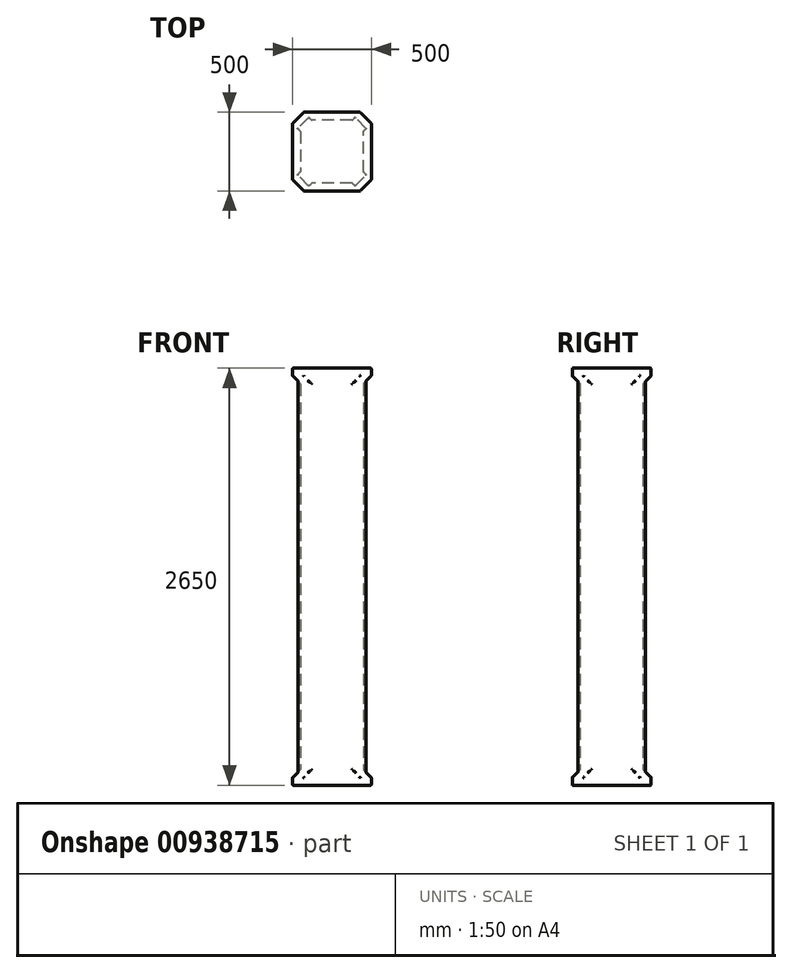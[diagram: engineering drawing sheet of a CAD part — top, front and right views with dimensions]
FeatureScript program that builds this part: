
annotation { "Feature Type Name" : "Feature", "Feature Type Description" : "" }
export const myFeature = defineFeature(function(context is Context, id is Id, definition is map)
    precondition{}
    {
        {
            var Q0;
            Q0=qCreatedBy(makeId("Top.planeOp"),FACE);
            var sketch = newSketch(context, id + "F0", { "sketchPlane" : qUnion([Q0])});
            skLineSegment(sketch, "E0.left", {"start": v(200, 129.29) * mm, "end": v(200, -129.29) * mm});
            skLineSegment(sketch, "E0.right", {"start": v(-200, 129.29) * mm, "end": v(-200, -129.29) * mm});
            skPoint(sketch, "E0.middle", {"position": v(0, 0) * mm});
            skLineSegment(sketch, "E1", {"start": v(-129.29, 200) * mm, "end": v(-146.97, 217.68) * mm});
            skLineSegment(sketch, "E2", {"start": v(-217.68, 146.97) * mm, "end": v(-200, 129.29) * mm});
            skLineSegment(sketch, "E3.1.0", {"start": v(-200, -129.29) * mm, "end": v(-217.68, -146.97) * mm});
            skLineSegment(sketch, "E3.1.3", {"start": v(-146.97, -217.68) * mm, "end": v(-129.29, -200) * mm});
            skLineSegment(sketch, "E3.2.0", {"start": v(129.29, -200) * mm, "end": v(146.97, -217.68) * mm});
            skLineSegment(sketch, "E3.2.3", {"start": v(217.68, -146.97) * mm, "end": v(200, -129.29) * mm});
            skLineSegment(sketch, "E3.3.0", {"start": v(200, 129.29) * mm, "end": v(217.68, 146.97) * mm});
            skLineSegment(sketch, "E3.3.3", {"start": v(146.97, 217.68) * mm, "end": v(129.29, 200) * mm});
            skLineSegment(sketch, "E4", {"start": v(-217.68, 146.97) * mm, "end": v(-146.97, 217.68) * mm});
            skLineSegment(sketch, "E5", {"start": v(0, 0) * mm, "end": v(-182.32, 182.32) * mm});
            skLineSegment(sketch, "E6", {"start": v(-217.68, -146.97) * mm, "end": v(-146.97, -217.68) * mm});
            skLineSegment(sketch, "E7", {"start": v(146.97, 217.68) * mm, "end": v(217.68, 146.97) * mm});
            skLineSegment(sketch, "E8", {"start": v(217.68, -146.97) * mm, "end": v(146.97, -217.68) * mm});
            skLineSegment(sketch, "E9.trimOffspring", {"start": v(129.29, -200) * mm, "end": v(-129.29, -200) * mm});
            skLineSegment(sketch, "E10.trimOffspring", {"start": v(129.29, 200) * mm, "end": v(-129.29, 200) * mm});
            skLineSegment(sketch, "E11", {"start": v(0, 0) * mm, "end": v(182.32, -182.32) * mm});
            skLineSegment(sketch, "E12", {"start": v(0, 0) * mm, "end": v(182.32, 182.32) * mm});
            skLineSegment(sketch, "E13", {"start": v(0, 0) * mm, "end": v(-182.32, -182.32) * mm});
            skSolve(sketch);
        }
        {
            var Q0;
            Q0 = qSketchRegion(id + "F0", true);
            extrude(context, id + "F1", {"entities" : qUnion([Q0]), "depth" : 1325 * mm, "offsetDistance" : 25 * mm});
        }
        {
            var Q0;
            Q0=qCreatedBy(makeId("Top.planeOp"),FACE);
            var sketch = newSketch(context, id + "F2", { "sketchPlane" : qUnion([Q0])});
            skPoint(sketch, "E14.middle", {"position": v(0, 0) * mm});
            skLineSegment(sketch, "E15", {"start": v(-179.29, 250) * mm, "end": v(179.29, 250) * mm});
            skLineSegment(sketch, "E16", {"start": v(179.29, 250) * mm, "end": v(250, 179.29) * mm});
            skLineSegment(sketch, "E17", {"start": v(250, 179.29) * mm, "end": v(250, -179.29) * mm});
            skLineSegment(sketch, "E18", {"start": v(250, -179.29) * mm, "end": v(179.29, -250) * mm});
            skLineSegment(sketch, "E19", {"start": v(179.29, -250) * mm, "end": v(-179.29, -250) * mm});
            skLineSegment(sketch, "E20", {"start": v(-179.29, -250) * mm, "end": v(-250, -179.29) * mm});
            skLineSegment(sketch, "E21", {"start": v(-250, -179.29) * mm, "end": v(-250, 179.29) * mm});
            skLineSegment(sketch, "E22", {"start": v(-250, 179.29) * mm, "end": v(-179.29, 250) * mm});
            skLineSegment(sketch, "E23", {"start": v(-214.64, -214.64) * mm, "end": v(214.64, 214.64) * mm});
            skLineSegment(sketch, "E24", {"start": v(214.64, -214.64) * mm, "end": v(-214.64, 214.64) * mm});
            skSolve(sketch);
        }
        {
            var Q0;
            Q0 = qSketchRegion(id + "F2", true);
            extrude(context, id + "F3", {"entities" : qUnion([Q0]), "depth" : 50 * mm, "offsetDistance" : 25 * mm});
        }
        {
            var Q0;
            Q0=qCreatedBy(makeId("Top.planeOp"),FACE);
            var sketch = newSketch(context, id + "F4", { "sketchPlane" : qUnion([Q0])});
            skLineSegment(sketch, "E25", {"start": v(-129.29, 200) * mm, "end": v(129.29, 200) * mm});
            skLineSegment(sketch, "E26", {"start": v(129.29, 200) * mm, "end": v(200, 129.29) * mm});
            skLineSegment(sketch, "E27", {"start": v(200, 129.29) * mm, "end": v(200, -129.29) * mm});
            skLineSegment(sketch, "E28", {"start": v(-129.29, -200) * mm, "end": v(-200, -129.29) * mm});
            skLineSegment(sketch, "E29", {"start": v(-200, -129.29) * mm, "end": v(-200, 129.29) * mm});
            skLineSegment(sketch, "E30", {"start": v(-200, 129.29) * mm, "end": v(-129.29, 200) * mm});
            skLineSegment(sketch, "E31", {"start": v(-129.29, -200) * mm, "end": v(129.29, -200) * mm});
            skLineSegment(sketch, "E32", {"start": v(129.29, -200) * mm, "end": v(200, -129.29) * mm});
            skLineSegment(sketch, "E33", {"start": v(-164.64, -164.64) * mm, "end": v(164.64, 164.64) * mm});
            skLineSegment(sketch, "E34", {"start": v(-164.64, 164.64) * mm, "end": v(164.64, -164.64) * mm});
            skPoint(sketch, "E35", {"position": v(0, 0) * mm});
            skSolve(sketch);
        }
        {
            var Q0;
            Q0 = qSketchRegion(id + "F4", true);
            extrude(context, id + "F5", {"entities" : qUnion([Q0]), "depth" : 100 * mm, "offsetDistance" : 25 * mm});
        }
        {
            var Q0;
            Q0=makeQuery(id+"F3.opExtrude","CAP_FACE",FACE,{"disambiguationData":[OSD([sQuery(id+"F2.wireOp",EDGE,"E15"),sQuery(id+"F2.wireOp",EDGE,"E16"),sQuery(id+"F2.wireOp",EDGE,"E17"),sQuery(id+"F2.wireOp",EDGE,"E18"),sQuery(id+"F2.wireOp",EDGE,"E19"),sQuery(id+"F2.wireOp",EDGE,"E20"),sQuery(id+"F2.wireOp",EDGE,"E21"),sQuery(id+"F2.wireOp",EDGE,"E22")])],"isStart":false});
            var Q1;
            Q1=makeQuery(id+"F5.opExtrude","CAP_FACE",FACE,{"disambiguationData":[OSD([sQuery(id+"F4.wireOp",EDGE,"E25"),sQuery(id+"F4.wireOp",EDGE,"E26"),sQuery(id+"F4.wireOp",EDGE,"E27"),sQuery(id+"F4.wireOp",EDGE,"E28"),sQuery(id+"F4.wireOp",EDGE,"E29"),sQuery(id+"F4.wireOp",EDGE,"E30"),sQuery(id+"F4.wireOp",EDGE,"E31"),sQuery(id+"F4.wireOp",EDGE,"E32")])],"isStart":false});
            loft(context, id + "F6", {"operationType" : NewBodyOperationType.ADD, "sheetProfilesArray" : [{ "sheetProfileEntities" : qUnion([Q0]) }, { "sheetProfileEntities" : qUnion([Q1]) }]});
        }
        {
            var Q0;
            Q0=makeQuery(id+"F5.opExtrude","SWEPT_BODY",BODY,{"disambiguationData":[OSD([sQuery(id+"F4.wireOp",EDGE,"E25"),sQuery(id+"F4.wireOp",EDGE,"E26"),sQuery(id+"F4.wireOp",EDGE,"E27"),sQuery(id+"F4.wireOp",EDGE,"E28"),sQuery(id+"F4.wireOp",EDGE,"E29"),sQuery(id+"F4.wireOp",EDGE,"E30"),sQuery(id+"F4.wireOp",EDGE,"E31"),sQuery(id+"F4.wireOp",EDGE,"E32")])]});
            var Q1;
            Q1=makeQuery(id+"F3.opExtrude","SWEPT_BODY",BODY,{"disambiguationData":[OSD([sQuery(id+"F2.wireOp",EDGE,"E15"),sQuery(id+"F2.wireOp",EDGE,"E16"),sQuery(id+"F2.wireOp",EDGE,"E17"),sQuery(id+"F2.wireOp",EDGE,"E18"),sQuery(id+"F2.wireOp",EDGE,"E19"),sQuery(id+"F2.wireOp",EDGE,"E20"),sQuery(id+"F2.wireOp",EDGE,"E21"),sQuery(id+"F2.wireOp",EDGE,"E22")])]});
            var Q2;
            Q2=makeQuery(id+"F1.opExtrude","SWEPT_BODY",BODY,{"disambiguationData":[OSD([sQuery(id+"F0.wireOp",EDGE,"E0.left"),sQuery(id+"F0.wireOp",EDGE,"E0.right"),sQuery(id+"F0.wireOp",EDGE,"E1"),sQuery(id+"F0.wireOp",EDGE,"E2"),sQuery(id+"F0.wireOp",EDGE,"E3.1.0"),sQuery(id+"F0.wireOp",EDGE,"E3.1.3"),sQuery(id+"F0.wireOp",EDGE,"E3.2.0"),sQuery(id+"F0.wireOp",EDGE,"E3.2.3"),sQuery(id+"F0.wireOp",EDGE,"E3.3.0"),sQuery(id+"F0.wireOp",EDGE,"E3.3.3"),sQuery(id+"F0.wireOp",EDGE,"E4"),sQuery(id+"F0.wireOp",EDGE,"E6"),sQuery(id+"F0.wireOp",EDGE,"E7"),sQuery(id+"F0.wireOp",EDGE,"E8"),sQuery(id+"F0.wireOp",EDGE,"E9.trimOffspring"),sQuery(id+"F0.wireOp",EDGE,"E10.trimOffspring")])]});
            var Q3;
            Q3=makeQuery(id+"F6.opLoft","SWEPT_BODY",BODY,{"disambiguationData":[OSD([sQuery(id+"F2.wireOp",EDGE,"E15"),sQuery(id+"F2.wireOp",EDGE,"E16"),sQuery(id+"F2.wireOp",EDGE,"E17"),sQuery(id+"F2.wireOp",EDGE,"E18"),sQuery(id+"F2.wireOp",EDGE,"E19"),sQuery(id+"F2.wireOp",EDGE,"E20"),sQuery(id+"F2.wireOp",EDGE,"E21"),sQuery(id+"F2.wireOp",EDGE,"E22"),sQuery(id+"F4.wireOp",EDGE,"E25"),sQuery(id+"F4.wireOp",EDGE,"E26"),sQuery(id+"F4.wireOp",EDGE,"E27"),sQuery(id+"F4.wireOp",EDGE,"E28"),sQuery(id+"F4.wireOp",EDGE,"E29"),sQuery(id+"F4.wireOp",EDGE,"E30"),sQuery(id+"F4.wireOp",EDGE,"E31"),sQuery(id+"F4.wireOp",EDGE,"E32")])]});
            var Q4;
            Q4=makeQuery(id+"F1.opExtrude","CAP_FACE",FACE,{"disambiguationData":[OSD([sQuery(id+"F0.wireOp",EDGE,"E0.left"),sQuery(id+"F0.wireOp",EDGE,"E0.right"),sQuery(id+"F0.wireOp",EDGE,"E1"),sQuery(id+"F0.wireOp",EDGE,"E2"),sQuery(id+"F0.wireOp",EDGE,"E3.1.0"),sQuery(id+"F0.wireOp",EDGE,"E3.1.3"),sQuery(id+"F0.wireOp",EDGE,"E3.2.0"),sQuery(id+"F0.wireOp",EDGE,"E3.2.3"),sQuery(id+"F0.wireOp",EDGE,"E3.3.0"),sQuery(id+"F0.wireOp",EDGE,"E3.3.3"),sQuery(id+"F0.wireOp",EDGE,"E4"),sQuery(id+"F0.wireOp",EDGE,"E6"),sQuery(id+"F0.wireOp",EDGE,"E7"),sQuery(id+"F0.wireOp",EDGE,"E8"),sQuery(id+"F0.wireOp",EDGE,"E9.trimOffspring"),sQuery(id+"F0.wireOp",EDGE,"E10.trimOffspring")])],"isStart":false});
            mirror(context, id + "F7", {"operationType" : NewBodyOperationType.ADD, "entities" : qUnion([Q0, Q1, Q2, Q3]), "mirrorPlane" : qUnion([Q4])});
        }
        {
            var Q0;
            Q0=makeQuery(id+"F5.opExtrude","CAP_FACE",FACE,{"disambiguationData":[OSD([sQuery(id+"F4.wireOp",EDGE,"E25"),sQuery(id+"F4.wireOp",EDGE,"E26"),sQuery(id+"F4.wireOp",EDGE,"E27"),sQuery(id+"F4.wireOp",EDGE,"E28"),sQuery(id+"F4.wireOp",EDGE,"E29"),sQuery(id+"F4.wireOp",EDGE,"E30"),sQuery(id+"F4.wireOp",EDGE,"E31"),sQuery(id+"F4.wireOp",EDGE,"E32")])],"isStart":false});
            var Q1;
            Q1=makeQuery(id+"F5.opExtrude","SWEPT_FACE",FACE,{"disambiguationData":[OSD([sQuery(id+"F4.wireOp",EDGE,"E31")])]});
            var Q2;
            Q2=makeQuery(id+"F5.opExtrude","CAP_EDGE",EDGE,{"disambiguationData":[OSD([sQuery(id+"F4.wireOp",EDGE,"E27")])],"isStart":false});
            var Q3;
            Q3=makeQuery(id+"F3.opExtrude","CAP_FACE",FACE,{"disambiguationData":[OSD([sQuery(id+"F2.wireOp",EDGE,"E15"),sQuery(id+"F2.wireOp",EDGE,"E16"),sQuery(id+"F2.wireOp",EDGE,"E17"),sQuery(id+"F2.wireOp",EDGE,"E18"),sQuery(id+"F2.wireOp",EDGE,"E19"),sQuery(id+"F2.wireOp",EDGE,"E20"),sQuery(id+"F2.wireOp",EDGE,"E21"),sQuery(id+"F2.wireOp",EDGE,"E22")])],"isStart":true});
            var Q4;
            Q4=makeQuery(id+"F3.opExtrude","CAP_FACE",FACE,{"disambiguationData":[OSD([sQuery(id+"F2.wireOp",EDGE,"E15"),sQuery(id+"F2.wireOp",EDGE,"E16"),sQuery(id+"F2.wireOp",EDGE,"E17"),sQuery(id+"F2.wireOp",EDGE,"E18"),sQuery(id+"F2.wireOp",EDGE,"E19"),sQuery(id+"F2.wireOp",EDGE,"E20"),sQuery(id+"F2.wireOp",EDGE,"E21"),sQuery(id+"F2.wireOp",EDGE,"E22")])],"isStart":false});
            var Q5;
            Q5=makeQuery(id+"F3.opExtrude","SWEPT_FACE",FACE,{"disambiguationData":[OSD([sQuery(id+"F2.wireOp",EDGE,"E16")])]});
            var Q6;
            Q6=makeQuery(id+"F3.opExtrude","SWEPT_FACE",FACE,{"disambiguationData":[OSD([sQuery(id+"F2.wireOp",EDGE,"E19")])]});
            var Q7;
            Q7=makeQuery(id+"F3.opExtrude","CAP_EDGE",EDGE,{"disambiguationData":[OSD([sQuery(id+"F2.wireOp",EDGE,"E17")])],"isStart":false});
            var Q8;
            Q8=makeQuery(id+"F3.opExtrude","SWEPT_FACE",FACE,{"disambiguationData":[OSD([sQuery(id+"F2.wireOp",EDGE,"E17")])]});
            var Q9;
            Q9=makeQuery(id+"F3.opExtrude","SWEPT_FACE",FACE,{"disambiguationData":[OSD([sQuery(id+"F2.wireOp",EDGE,"E18")])]});
            var Q10;
            Q10=makeQuery(id+"F3.opExtrude","CAP_EDGE",EDGE,{"disambiguationData":[OSD([sQuery(id+"F2.wireOp",EDGE,"E17")])],"isStart":true});
            var Q11;
            {var subQ0=makeQuery(id+"F1.opExtrude","SWEPT_FACE",FACE,{"disambiguationData":[OSD([sQuery(id+"F0.wireOp",EDGE,"E3.1.0")])]});Q11=makeQuery(id+"F7.boolean.opBoolean","MERGE",FACE,{"derivedFrom":[subQ0,makeQuery(id+"F7.opPattern","COPY",FACE,{"derivedFrom":subQ0,"instanceName":"1"})]});}
            var Q12;
            Q12=makeQuery(id+"F7.opPattern","COPY",EDGE,{"derivedFrom":makeQuery(id+"F3.opExtrude","CAP_EDGE",EDGE,{"disambiguationData":[OSD([sQuery(id+"F2.wireOp",EDGE,"E21")])],"isStart":true}),"instanceName":"1"});
            var Q13;
            {var subQ0=makeQuery(id+"F1.opExtrude","SWEPT_EDGE",EDGE,{"disambiguationData":[OSD([sQuery(id+"F0.wireOp",EDGE,"E3.3.0"),sQuery(id+"F0.wireOp",EDGE,"E7")])]});Q13=makeQuery(id+"F7.boolean.opBoolean","MERGE",EDGE,{"derivedFrom":[subQ0,makeQuery(id+"F7.opPattern","COPY",EDGE,{"derivedFrom":subQ0,"instanceName":"1"})]});}
            var Q14;
            {var subQ0=makeQuery(id+"F1.opExtrude","SWEPT_EDGE",EDGE,{"disambiguationData":[OSD([sQuery(id+"F0.wireOp",EDGE,"E3.2.3"),sQuery(id+"F0.wireOp",EDGE,"E8")])]});Q14=makeQuery(id+"F7.boolean.opBoolean","MERGE",EDGE,{"derivedFrom":[subQ0,makeQuery(id+"F7.opPattern","COPY",EDGE,{"derivedFrom":subQ0,"instanceName":"1"})]});}
            var Q15;
            {var subQ0=makeQuery(id+"F1.opExtrude","SWEPT_FACE",FACE,{"disambiguationData":[OSD([sQuery(id+"F0.wireOp",EDGE,"E3.2.0")])]});Q15=makeQuery(id+"F7.boolean.opBoolean","MERGE",FACE,{"derivedFrom":[subQ0,makeQuery(id+"F7.opPattern","COPY",FACE,{"derivedFrom":subQ0,"instanceName":"1"})]});}
            var Q16;
            {var subQ0=makeQuery(id+"F1.opExtrude","SWEPT_EDGE",EDGE,{"disambiguationData":[OSD([sQuery(id+"F0.wireOp",EDGE,"E3.1.3"),sQuery(id+"F0.wireOp",EDGE,"E6")])]});Q16=makeQuery(id+"F7.boolean.opBoolean","MERGE",EDGE,{"derivedFrom":[subQ0,makeQuery(id+"F7.opPattern","COPY",EDGE,{"derivedFrom":subQ0,"instanceName":"1"})]});}
            var Q17;
            {var subQ0=makeQuery(id+"F1.opExtrude","SWEPT_FACE",FACE,{"disambiguationData":[OSD([sQuery(id+"F0.wireOp",EDGE,"E7")])]});Q17=makeQuery(id+"F7.boolean.opBoolean","MERGE",FACE,{"derivedFrom":[subQ0,makeQuery(id+"F7.opPattern","COPY",FACE,{"derivedFrom":subQ0,"instanceName":"1"})]});}
            var Q18;
            {var subQ0=makeQuery(id+"F1.opExtrude","SWEPT_EDGE",EDGE,{"disambiguationData":[OSD([sQuery(id+"F0.wireOp",EDGE,"E0.left"),sQuery(id+"F0.wireOp",EDGE,"E3.3.0")])]});Q18=makeQuery(id+"F7.boolean.opBoolean","MERGE",EDGE,{"derivedFrom":[subQ0,makeQuery(id+"F7.opPattern","COPY",EDGE,{"derivedFrom":subQ0,"instanceName":"1"})]});}
            var Q19;
            {var subQ0=makeQuery(id+"F1.opExtrude","SWEPT_EDGE",EDGE,{"disambiguationData":[OSD([sQuery(id+"F0.wireOp",EDGE,"E3.1.3"),sQuery(id+"F0.wireOp",EDGE,"E9.trimOffspring")])]});Q19=makeQuery(id+"F7.boolean.opBoolean","MERGE",EDGE,{"derivedFrom":[subQ0,makeQuery(id+"F7.opPattern","COPY",EDGE,{"derivedFrom":subQ0,"instanceName":"1"})]});}
            var Q20;
            Q20=makeQuery(id+"F7.opPattern","COPY",FACE,{"derivedFrom":makeQuery(id+"F3.opExtrude","SWEPT_FACE",FACE,{"disambiguationData":[OSD([sQuery(id+"F2.wireOp",EDGE,"E16")])]}),"instanceName":"1"});
            var Q21;
            {var subQ0=makeQuery(id+"F1.opExtrude","SWEPT_FACE",FACE,{"disambiguationData":[OSD([sQuery(id+"F0.wireOp",EDGE,"E3.1.3")])]});Q21=makeQuery(id+"F7.boolean.opBoolean","MERGE",FACE,{"derivedFrom":[subQ0,makeQuery(id+"F7.opPattern","COPY",FACE,{"derivedFrom":subQ0,"instanceName":"1"})]});}
            var Q22;
            {var subQ0=makeQuery(id+"F1.opExtrude","SWEPT_FACE",FACE,{"disambiguationData":[OSD([sQuery(id+"F0.wireOp",EDGE,"E9.trimOffspring")])]});Q22=makeQuery(id+"F7.boolean.opBoolean","MERGE",FACE,{"derivedFrom":[subQ0,makeQuery(id+"F7.opPattern","COPY",FACE,{"derivedFrom":subQ0,"instanceName":"1"})]});}
            var Q23;
            {var subQ0=makeQuery(id+"F1.opExtrude","SWEPT_FACE",FACE,{"disambiguationData":[OSD([sQuery(id+"F0.wireOp",EDGE,"E3.3.0")])]});Q23=makeQuery(id+"F7.boolean.opBoolean","MERGE",FACE,{"derivedFrom":[subQ0,makeQuery(id+"F7.opPattern","COPY",FACE,{"derivedFrom":subQ0,"instanceName":"1"})]});}
            var Q24;
            {var subQ0=makeQuery(id+"F1.opExtrude","SWEPT_FACE",FACE,{"disambiguationData":[OSD([sQuery(id+"F0.wireOp",EDGE,"E0.left")])]});Q24=makeQuery(id+"F7.boolean.opBoolean","MERGE",FACE,{"derivedFrom":[subQ0,makeQuery(id+"F7.opPattern","COPY",FACE,{"derivedFrom":subQ0,"instanceName":"1"})]});}
            var Q25;
            {var subQ0=makeQuery(id+"F1.opExtrude","SWEPT_FACE",FACE,{"disambiguationData":[OSD([sQuery(id+"F0.wireOp",EDGE,"E6")])]});Q25=makeQuery(id+"F7.boolean.opBoolean","MERGE",FACE,{"derivedFrom":[subQ0,makeQuery(id+"F7.opPattern","COPY",FACE,{"derivedFrom":subQ0,"instanceName":"1"})]});}
            var Q26;
            {var subQ0=makeQuery(id+"F1.opExtrude","SWEPT_EDGE",EDGE,{"disambiguationData":[OSD([sQuery(id+"F0.wireOp",EDGE,"E3.2.0"),sQuery(id+"F0.wireOp",EDGE,"E8")])]});Q26=makeQuery(id+"F7.boolean.opBoolean","MERGE",EDGE,{"derivedFrom":[subQ0,makeQuery(id+"F7.opPattern","COPY",EDGE,{"derivedFrom":subQ0,"instanceName":"1"})]});}
            var Q27;
            Q27=makeQuery(id+"F7.opPattern","COPY",FACE,{"derivedFrom":makeQuery(id+"F3.opExtrude","SWEPT_FACE",FACE,{"disambiguationData":[OSD([sQuery(id+"F2.wireOp",EDGE,"E17")])]}),"instanceName":"1"});
            var Q28;
            {var subQ0=makeQuery(id+"F1.opExtrude","SWEPT_EDGE",EDGE,{"disambiguationData":[OSD([sQuery(id+"F0.wireOp",EDGE,"E3.2.0"),sQuery(id+"F0.wireOp",EDGE,"E9.trimOffspring")])]});Q28=makeQuery(id+"F7.boolean.opBoolean","MERGE",EDGE,{"derivedFrom":[subQ0,makeQuery(id+"F7.opPattern","COPY",EDGE,{"derivedFrom":subQ0,"instanceName":"1"})]});}
            var Q29;
            {var subQ0=makeQuery(id+"F1.opExtrude","SWEPT_EDGE",EDGE,{"disambiguationData":[OSD([sQuery(id+"F0.wireOp",EDGE,"E3.1.0"),sQuery(id+"F0.wireOp",EDGE,"E6")])]});Q29=makeQuery(id+"F7.boolean.opBoolean","MERGE",EDGE,{"derivedFrom":[subQ0,makeQuery(id+"F7.opPattern","COPY",EDGE,{"derivedFrom":subQ0,"instanceName":"1"})]});}
            var Q30;
            Q30=makeQuery(id+"F7.opPattern","COPY",FACE,{"derivedFrom":makeQuery(id+"F3.opExtrude","SWEPT_FACE",FACE,{"disambiguationData":[OSD([sQuery(id+"F2.wireOp",EDGE,"E15")])]}),"instanceName":"1"});
            var Q31;
            {var subQ0=makeQuery(id+"F1.opExtrude","SWEPT_FACE",FACE,{"disambiguationData":[OSD([sQuery(id+"F0.wireOp",EDGE,"E8")])]});Q31=makeQuery(id+"F7.boolean.opBoolean","MERGE",FACE,{"derivedFrom":[subQ0,makeQuery(id+"F7.opPattern","COPY",FACE,{"derivedFrom":subQ0,"instanceName":"1"})]});}
            var Q32;
            {var subQ0=makeQuery(id+"F1.opExtrude","SWEPT_FACE",FACE,{"disambiguationData":[OSD([sQuery(id+"F0.wireOp",EDGE,"E3.2.3")])]});Q32=makeQuery(id+"F7.boolean.opBoolean","MERGE",FACE,{"derivedFrom":[subQ0,makeQuery(id+"F7.opPattern","COPY",FACE,{"derivedFrom":subQ0,"instanceName":"1"})]});}
            var Q33;
            Q33=makeQuery(id+"F7.opPattern","COPY",FACE,{"derivedFrom":makeQuery(id+"F3.opExtrude","SWEPT_FACE",FACE,{"disambiguationData":[OSD([sQuery(id+"F2.wireOp",EDGE,"E18")])]}),"instanceName":"1"});
            var Q34;
            Q34=makeQuery(id+"F7.opPattern","COPY",EDGE,{"derivedFrom":makeQuery(id+"F3.opExtrude","CAP_EDGE",EDGE,{"disambiguationData":[OSD([sQuery(id+"F2.wireOp",EDGE,"E15")])],"isStart":true}),"instanceName":"1"});
            var Q35;
            Q35=makeQuery(id+"F7.opPattern","COPY",FACE,{"derivedFrom":makeQuery(id+"F3.opExtrude","SWEPT_FACE",FACE,{"disambiguationData":[OSD([sQuery(id+"F2.wireOp",EDGE,"E19")])]}),"instanceName":"1"});
            var Q36;
            Q36=makeQuery(id+"F7.opPattern","COPY",FACE,{"derivedFrom":makeQuery(id+"F3.opExtrude","SWEPT_FACE",FACE,{"disambiguationData":[OSD([sQuery(id+"F2.wireOp",EDGE,"E20")])]}),"instanceName":"1"});
            var Q37;
            Q37=makeQuery(id+"F7.opPattern","COPY",FACE,{"derivedFrom":makeQuery(id+"F3.opExtrude","SWEPT_FACE",FACE,{"disambiguationData":[OSD([sQuery(id+"F2.wireOp",EDGE,"E21")])]}),"instanceName":"1"});
            var Q38;
            Q38=makeQuery(id+"F7.opPattern","COPY",FACE,{"derivedFrom":makeQuery(id+"F3.opExtrude","SWEPT_FACE",FACE,{"disambiguationData":[OSD([sQuery(id+"F2.wireOp",EDGE,"E22")])]}),"instanceName":"1"});
            var Q39;
            Q39=makeQuery(id+"F7.opPattern","COPY",FACE,{"derivedFrom":makeQuery(id+"F6.opLoft","SWEPT_FACE",FACE,{"disambiguationData":[OSD([sQuery(id+"F2.wireOp",EDGE,"E18"),sQuery(id+"F2.wireOp",EDGE,"E19"),sQuery(id+"F2.wireOp",EDGE,"E20"),sQuery(id+"F4.wireOp",EDGE,"E28"),sQuery(id+"F4.wireOp",EDGE,"E31"),sQuery(id+"F4.wireOp",EDGE,"E32")])]}),"instanceName":"1"});
            var Q40;
            Q40=makeQuery(id+"F7.opPattern","COPY",EDGE,{"derivedFrom":makeQuery(id+"F3.opExtrude","CAP_EDGE",EDGE,{"disambiguationData":[OSD([sQuery(id+"F2.wireOp",EDGE,"E17")])],"isStart":true}),"instanceName":"1"});
            var Q41;
            Q41=makeQuery(id+"F7.boolean.opBoolean","MERGE",FACE,{"derivedFrom":[makeQuery(id+"F7.opPattern","COPY",FACE,{"derivedFrom":makeQuery(id+"F1.opExtrude","CAP_FACE",FACE,{"disambiguationData":[OSD([sQuery(id+"F0.wireOp",EDGE,"E0.left"),sQuery(id+"F0.wireOp",EDGE,"E0.right"),sQuery(id+"F0.wireOp",EDGE,"E1"),sQuery(id+"F0.wireOp",EDGE,"E2"),sQuery(id+"F0.wireOp",EDGE,"E3.1.0"),sQuery(id+"F0.wireOp",EDGE,"E3.1.3"),sQuery(id+"F0.wireOp",EDGE,"E3.2.0"),sQuery(id+"F0.wireOp",EDGE,"E3.2.3"),sQuery(id+"F0.wireOp",EDGE,"E3.3.0"),sQuery(id+"F0.wireOp",EDGE,"E3.3.3"),sQuery(id+"F0.wireOp",EDGE,"E4"),sQuery(id+"F0.wireOp",EDGE,"E6"),sQuery(id+"F0.wireOp",EDGE,"E7"),sQuery(id+"F0.wireOp",EDGE,"E8"),sQuery(id+"F0.wireOp",EDGE,"E9.trimOffspring"),sQuery(id+"F0.wireOp",EDGE,"E10.trimOffspring")])],"isStart":true}),"instanceName":"1"}),makeQuery(id+"F7.opPattern","COPY",FACE,{"derivedFrom":makeQuery(id+"F3.opExtrude","CAP_FACE",FACE,{"disambiguationData":[OSD([sQuery(id+"F2.wireOp",EDGE,"E15"),sQuery(id+"F2.wireOp",EDGE,"E16"),sQuery(id+"F2.wireOp",EDGE,"E17"),sQuery(id+"F2.wireOp",EDGE,"E18"),sQuery(id+"F2.wireOp",EDGE,"E19"),sQuery(id+"F2.wireOp",EDGE,"E20"),sQuery(id+"F2.wireOp",EDGE,"E21"),sQuery(id+"F2.wireOp",EDGE,"E22")])],"isStart":true}),"instanceName":"1"})]});
            var Q42;
            Q42=makeQuery(id+"F6.opLoft","SWEPT_FACE",FACE,{"disambiguationData":[OSD([sQuery(id+"F2.wireOp",EDGE,"E16"),sQuery(id+"F2.wireOp",EDGE,"E17"),sQuery(id+"F2.wireOp",EDGE,"E18"),sQuery(id+"F4.wireOp",EDGE,"E26"),sQuery(id+"F4.wireOp",EDGE,"E27"),sQuery(id+"F4.wireOp",EDGE,"E32")])]});
            var Q43;
            Q43=makeQuery(id+"F6.opLoft","SWEPT_FACE",FACE,{"disambiguationData":[OSD([sQuery(id+"F2.wireOp",EDGE,"E17"),sQuery(id+"F2.wireOp",EDGE,"E18"),sQuery(id+"F2.wireOp",EDGE,"E19"),sQuery(id+"F4.wireOp",EDGE,"E27"),sQuery(id+"F4.wireOp",EDGE,"E31"),sQuery(id+"F4.wireOp",EDGE,"E32")])]});
            var Q44;
            Q44=makeQuery(id+"F6.opLoft","SWEPT_FACE",FACE,{"disambiguationData":[OSD([sQuery(id+"F2.wireOp",EDGE,"E19"),sQuery(id+"F2.wireOp",EDGE,"E20"),sQuery(id+"F2.wireOp",EDGE,"E21"),sQuery(id+"F4.wireOp",EDGE,"E28"),sQuery(id+"F4.wireOp",EDGE,"E29"),sQuery(id+"F4.wireOp",EDGE,"E31")])]});
            var Q45;
            Q45=makeQuery(id+"F6.opLoft","CAP_FACE",FACE,{"disambiguationData":[OSD([sQuery(id+"F2.wireOp",EDGE,"E15"),sQuery(id+"F2.wireOp",EDGE,"E16"),sQuery(id+"F2.wireOp",EDGE,"E17"),sQuery(id+"F2.wireOp",EDGE,"E18"),sQuery(id+"F2.wireOp",EDGE,"E19"),sQuery(id+"F2.wireOp",EDGE,"E20"),sQuery(id+"F2.wireOp",EDGE,"E21"),sQuery(id+"F2.wireOp",EDGE,"E22")])],"isStart":true});
            var Q46;
            Q46=makeQuery(id+"F6.opLoft","SWEPT_FACE",FACE,{"disambiguationData":[OSD([sQuery(id+"F2.wireOp",EDGE,"E18"),sQuery(id+"F2.wireOp",EDGE,"E19"),sQuery(id+"F2.wireOp",EDGE,"E20"),sQuery(id+"F4.wireOp",EDGE,"E28"),sQuery(id+"F4.wireOp",EDGE,"E31"),sQuery(id+"F4.wireOp",EDGE,"E32")])]});
            var Q47;
            Q47=makeQuery(id+"F5.opExtrude","SWEPT_EDGE",EDGE,{"disambiguationData":[OSD([sQuery(id+"F4.wireOp",EDGE,"E28"),sQuery(id+"F4.wireOp",EDGE,"E31")])]});
            var Q48;
            Q48=makeQuery(id+"F5.opExtrude","SWEPT_FACE",FACE,{"disambiguationData":[OSD([sQuery(id+"F4.wireOp",EDGE,"E25")])]});
            var Q49;
            Q49=makeQuery(id+"F5.opExtrude","SWEPT_EDGE",EDGE,{"disambiguationData":[OSD([sQuery(id+"F4.wireOp",EDGE,"E28"),sQuery(id+"F4.wireOp",EDGE,"E29")])]});
            var Q50;
            Q50=makeQuery(id+"F5.opExtrude","SWEPT_FACE",FACE,{"disambiguationData":[OSD([sQuery(id+"F4.wireOp",EDGE,"E28")])]});
            var Q51;
            Q51=makeQuery(id+"F5.opExtrude","CAP_EDGE",EDGE,{"disambiguationData":[OSD([sQuery(id+"F4.wireOp",EDGE,"E26")])],"isStart":false});
            var Q52;
            Q52=makeQuery(id+"F5.opExtrude","SWEPT_FACE",FACE,{"disambiguationData":[OSD([sQuery(id+"F4.wireOp",EDGE,"E29")])]});
            var Q53;
            Q53=makeQuery(id+"F5.opExtrude","CAP_FACE",FACE,{"disambiguationData":[OSD([sQuery(id+"F4.wireOp",EDGE,"E25"),sQuery(id+"F4.wireOp",EDGE,"E26"),sQuery(id+"F4.wireOp",EDGE,"E27"),sQuery(id+"F4.wireOp",EDGE,"E28"),sQuery(id+"F4.wireOp",EDGE,"E29"),sQuery(id+"F4.wireOp",EDGE,"E30"),sQuery(id+"F4.wireOp",EDGE,"E31"),sQuery(id+"F4.wireOp",EDGE,"E32")])],"isStart":true});
            var Q54;
            Q54=makeQuery(id+"F5.opExtrude","SWEPT_FACE",FACE,{"disambiguationData":[OSD([sQuery(id+"F4.wireOp",EDGE,"E32")])]});
            var Q55;
            Q55=makeQuery(id+"F5.opExtrude","SWEPT_FACE",FACE,{"disambiguationData":[OSD([sQuery(id+"F4.wireOp",EDGE,"E27")])]});
            var Q56;
            Q56=makeQuery(id+"F5.opExtrude","CAP_EDGE",EDGE,{"disambiguationData":[OSD([sQuery(id+"F4.wireOp",EDGE,"E29")])],"isStart":false});
            var Q57;
            Q57=makeQuery(id+"F5.opExtrude","SWEPT_FACE",FACE,{"disambiguationData":[OSD([sQuery(id+"F4.wireOp",EDGE,"E26")])]});
            var Q58;
            Q58=makeQuery(id+"F5.opExtrude","SWEPT_EDGE",EDGE,{"disambiguationData":[OSD([sQuery(id+"F4.wireOp",EDGE,"E26"),sQuery(id+"F4.wireOp",EDGE,"E27")])]});
            var Q59;
            Q59=makeQuery(id+"F5.opExtrude","CAP_EDGE",EDGE,{"disambiguationData":[OSD([sQuery(id+"F4.wireOp",EDGE,"E31")])],"isStart":false});
            var Q60;
            Q60=makeQuery(id+"F5.opExtrude","SWEPT_FACE",FACE,{"disambiguationData":[OSD([sQuery(id+"F4.wireOp",EDGE,"E30")])]});
            var Q61;
            Q61=makeQuery(id+"F3.opExtrude","CAP_EDGE",EDGE,{"disambiguationData":[OSD([sQuery(id+"F2.wireOp",EDGE,"E18")])],"isStart":true});
            var Q62;
            Q62=makeQuery(id+"F3.opExtrude","CAP_EDGE",EDGE,{"disambiguationData":[OSD([sQuery(id+"F2.wireOp",EDGE,"E16")])],"isStart":true});
            var Q63;
            Q63=makeQuery(id+"F3.opExtrude","SWEPT_FACE",FACE,{"disambiguationData":[OSD([sQuery(id+"F2.wireOp",EDGE,"E21")])]});
            var Q64;
            Q64=makeQuery(id+"F3.opExtrude","CAP_EDGE",EDGE,{"disambiguationData":[OSD([sQuery(id+"F2.wireOp",EDGE,"E19")])],"isStart":false});
            var Q65;
            Q65=makeQuery(id+"F3.opExtrude","CAP_EDGE",EDGE,{"disambiguationData":[OSD([sQuery(id+"F2.wireOp",EDGE,"E19")])],"isStart":true});
            var Q66;
            Q66=makeQuery(id+"F3.opExtrude","SWEPT_EDGE",EDGE,{"disambiguationData":[OSD([sQuery(id+"F2.wireOp",EDGE,"E19"),sQuery(id+"F2.wireOp",EDGE,"E20")])]});
            var Q67;
            Q67=makeQuery(id+"F3.opExtrude","CAP_EDGE",EDGE,{"disambiguationData":[OSD([sQuery(id+"F2.wireOp",EDGE,"E18")])],"isStart":false});
            var Q68;
            Q68=makeQuery(id+"F3.opExtrude","SWEPT_FACE",FACE,{"disambiguationData":[OSD([sQuery(id+"F2.wireOp",EDGE,"E20")])]});
            var Q69;
            Q69=makeQuery(id+"F3.opExtrude","SWEPT_EDGE",EDGE,{"disambiguationData":[OSD([sQuery(id+"F2.wireOp",EDGE,"E16"),sQuery(id+"F2.wireOp",EDGE,"E17")])]});
            var Q70;
            Q70=makeQuery(id+"F7.opPattern","COPY",EDGE,{"derivedFrom":makeQuery(id+"F3.opExtrude","SWEPT_EDGE",EDGE,{"disambiguationData":[OSD([sQuery(id+"F2.wireOp",EDGE,"E20"),sQuery(id+"F2.wireOp",EDGE,"E21")])]}),"instanceName":"1"});
            var Q71;
            Q71=makeQuery(id+"F7.opPattern","COPY",EDGE,{"derivedFrom":makeQuery(id+"F3.opExtrude","CAP_EDGE",EDGE,{"disambiguationData":[OSD([sQuery(id+"F2.wireOp",EDGE,"E19")])],"isStart":true}),"instanceName":"1"});
            var Q72;
            Q72=makeQuery(id+"F7.opPattern","COPY",FACE,{"derivedFrom":makeQuery(id+"F6.opLoft","SWEPT_FACE",FACE,{"disambiguationData":[OSD([sQuery(id+"F2.wireOp",EDGE,"E15"),sQuery(id+"F2.wireOp",EDGE,"E16"),sQuery(id+"F2.wireOp",EDGE,"E22"),sQuery(id+"F4.wireOp",EDGE,"E25"),sQuery(id+"F4.wireOp",EDGE,"E26"),sQuery(id+"F4.wireOp",EDGE,"E30")])]}),"instanceName":"1"});
            var Q73;
            {var subQ0=makeQuery(id+"F1.opExtrude","SWEPT_EDGE",EDGE,{"disambiguationData":[OSD([sQuery(id+"F0.wireOp",EDGE,"E0.right"),sQuery(id+"F0.wireOp",EDGE,"E2")])]});Q73=makeQuery(id+"F7.boolean.opBoolean","MERGE",EDGE,{"derivedFrom":[subQ0,makeQuery(id+"F7.opPattern","COPY",EDGE,{"derivedFrom":subQ0,"instanceName":"1"})]});}
            var Q74;
            {var subQ0=makeQuery(id+"F1.opExtrude","SWEPT_EDGE",EDGE,{"disambiguationData":[OSD([sQuery(id+"F0.wireOp",EDGE,"E0.right"),sQuery(id+"F0.wireOp",EDGE,"E3.1.0")])]});Q74=makeQuery(id+"F7.boolean.opBoolean","MERGE",EDGE,{"derivedFrom":[subQ0,makeQuery(id+"F7.opPattern","COPY",EDGE,{"derivedFrom":subQ0,"instanceName":"1"})]});}
            var Q75;
            {var subQ0=makeQuery(id+"F1.opExtrude","SWEPT_FACE",FACE,{"disambiguationData":[OSD([sQuery(id+"F0.wireOp",EDGE,"E3.3.3")])]});Q75=makeQuery(id+"F7.boolean.opBoolean","MERGE",FACE,{"derivedFrom":[subQ0,makeQuery(id+"F7.opPattern","COPY",FACE,{"derivedFrom":subQ0,"instanceName":"1"})]});}
            var Q76;
            {var subQ0=makeQuery(id+"F1.opExtrude","SWEPT_EDGE",EDGE,{"disambiguationData":[OSD([sQuery(id+"F0.wireOp",EDGE,"E1"),sQuery(id+"F0.wireOp",EDGE,"E10.trimOffspring")])]});Q76=makeQuery(id+"F7.boolean.opBoolean","MERGE",EDGE,{"derivedFrom":[subQ0,makeQuery(id+"F7.opPattern","COPY",EDGE,{"derivedFrom":subQ0,"instanceName":"1"})]});}
            var Q77;
            Q77=makeQuery(id+"F7.opPattern","COPY",EDGE,{"derivedFrom":makeQuery(id+"F3.opExtrude","SWEPT_EDGE",EDGE,{"disambiguationData":[OSD([sQuery(id+"F2.wireOp",EDGE,"E15"),sQuery(id+"F2.wireOp",EDGE,"E22")])]}),"instanceName":"1"});
            var Q78;
            {var subQ0=makeQuery(id+"F1.opExtrude","SWEPT_FACE",FACE,{"disambiguationData":[OSD([sQuery(id+"F0.wireOp",EDGE,"E10.trimOffspring")])]});Q78=makeQuery(id+"F7.boolean.opBoolean","MERGE",FACE,{"derivedFrom":[subQ0,makeQuery(id+"F7.opPattern","COPY",FACE,{"derivedFrom":subQ0,"instanceName":"1"})]});}
            var Q79;
            Q79=makeQuery(id+"F7.opPattern","COPY",FACE,{"derivedFrom":makeQuery(id+"F6.opLoft","SWEPT_FACE",FACE,{"disambiguationData":[OSD([sQuery(id+"F2.wireOp",EDGE,"E20"),sQuery(id+"F2.wireOp",EDGE,"E21"),sQuery(id+"F2.wireOp",EDGE,"E22"),sQuery(id+"F4.wireOp",EDGE,"E28"),sQuery(id+"F4.wireOp",EDGE,"E29"),sQuery(id+"F4.wireOp",EDGE,"E30")])]}),"instanceName":"1"});
            var Q80;
            {var subQ0=makeQuery(id+"F1.opExtrude","SWEPT_FACE",FACE,{"disambiguationData":[OSD([sQuery(id+"F0.wireOp",EDGE,"E4")])]});Q80=makeQuery(id+"F7.boolean.opBoolean","MERGE",FACE,{"derivedFrom":[subQ0,makeQuery(id+"F7.opPattern","COPY",FACE,{"derivedFrom":subQ0,"instanceName":"1"})]});}
            var Q81;
            Q81=makeQuery(id+"F7.opPattern","COPY",EDGE,{"derivedFrom":makeQuery(id+"F3.opExtrude","SWEPT_EDGE",EDGE,{"disambiguationData":[OSD([sQuery(id+"F2.wireOp",EDGE,"E18"),sQuery(id+"F2.wireOp",EDGE,"E19")])]}),"instanceName":"1"});
            var Q82;
            Q82=makeQuery(id+"F7.opPattern","COPY",EDGE,{"derivedFrom":makeQuery(id+"F3.opExtrude","CAP_EDGE",EDGE,{"disambiguationData":[OSD([sQuery(id+"F2.wireOp",EDGE,"E20")])],"isStart":true}),"instanceName":"1"});
            var Q83;
            Q83=makeQuery(id+"F7.opPattern","COPY",EDGE,{"derivedFrom":makeQuery(id+"F3.opExtrude","SWEPT_EDGE",EDGE,{"disambiguationData":[OSD([sQuery(id+"F2.wireOp",EDGE,"E19"),sQuery(id+"F2.wireOp",EDGE,"E20")])]}),"instanceName":"1"});
            var Q84;
            Q84=makeQuery(id+"F7.opPattern","COPY",EDGE,{"derivedFrom":makeQuery(id+"F3.opExtrude","SWEPT_EDGE",EDGE,{"disambiguationData":[OSD([sQuery(id+"F2.wireOp",EDGE,"E15"),sQuery(id+"F2.wireOp",EDGE,"E16")])]}),"instanceName":"1"});
            var Q85;
            Q85=makeQuery(id+"F7.opPattern","COPY",EDGE,{"derivedFrom":makeQuery(id+"F3.opExtrude","CAP_EDGE",EDGE,{"disambiguationData":[OSD([sQuery(id+"F2.wireOp",EDGE,"E22")])],"isStart":true}),"instanceName":"1"});
            var Q86;
            {var subQ0=makeQuery(id+"F1.opExtrude","SWEPT_EDGE",EDGE,{"disambiguationData":[OSD([sQuery(id+"F0.wireOp",EDGE,"E0.left"),sQuery(id+"F0.wireOp",EDGE,"E3.2.3")])]});Q86=makeQuery(id+"F7.boolean.opBoolean","MERGE",EDGE,{"derivedFrom":[subQ0,makeQuery(id+"F7.opPattern","COPY",EDGE,{"derivedFrom":subQ0,"instanceName":"1"})]});}
            var Q87;
            {var subQ0=makeQuery(id+"F1.opExtrude","SWEPT_EDGE",EDGE,{"disambiguationData":[OSD([sQuery(id+"F0.wireOp",EDGE,"E3.3.3"),sQuery(id+"F0.wireOp",EDGE,"E7")])]});Q87=makeQuery(id+"F7.boolean.opBoolean","MERGE",EDGE,{"derivedFrom":[subQ0,makeQuery(id+"F7.opPattern","COPY",EDGE,{"derivedFrom":subQ0,"instanceName":"1"})]});}
            var Q88;
            Q88=makeQuery(id+"F1.opExtrude","CAP_FACE",FACE,{"disambiguationData":[OSD([sQuery(id+"F0.wireOp",EDGE,"E0.left"),sQuery(id+"F0.wireOp",EDGE,"E0.right"),sQuery(id+"F0.wireOp",EDGE,"E1"),sQuery(id+"F0.wireOp",EDGE,"E2"),sQuery(id+"F0.wireOp",EDGE,"E3.1.0"),sQuery(id+"F0.wireOp",EDGE,"E3.1.3"),sQuery(id+"F0.wireOp",EDGE,"E3.2.0"),sQuery(id+"F0.wireOp",EDGE,"E3.2.3"),sQuery(id+"F0.wireOp",EDGE,"E3.3.0"),sQuery(id+"F0.wireOp",EDGE,"E3.3.3"),sQuery(id+"F0.wireOp",EDGE,"E4"),sQuery(id+"F0.wireOp",EDGE,"E6"),sQuery(id+"F0.wireOp",EDGE,"E7"),sQuery(id+"F0.wireOp",EDGE,"E8"),sQuery(id+"F0.wireOp",EDGE,"E9.trimOffspring"),sQuery(id+"F0.wireOp",EDGE,"E10.trimOffspring")])],"isStart":true});
            var Q89;
            {var subQ0=makeQuery(id+"F1.opExtrude","SWEPT_FACE",FACE,{"disambiguationData":[OSD([sQuery(id+"F0.wireOp",EDGE,"E2")])]});Q89=makeQuery(id+"F7.boolean.opBoolean","MERGE",FACE,{"derivedFrom":[subQ0,makeQuery(id+"F7.opPattern","COPY",FACE,{"derivedFrom":subQ0,"instanceName":"1"})]});}
            var Q90;
            {var subQ0=makeQuery(id+"F1.opExtrude","SWEPT_EDGE",EDGE,{"disambiguationData":[OSD([sQuery(id+"F0.wireOp",EDGE,"E1"),sQuery(id+"F0.wireOp",EDGE,"E4")])]});Q90=makeQuery(id+"F7.boolean.opBoolean","MERGE",EDGE,{"derivedFrom":[subQ0,makeQuery(id+"F7.opPattern","COPY",EDGE,{"derivedFrom":subQ0,"instanceName":"1"})]});}
            var Q91;
            {var subQ0=makeQuery(id+"F1.opExtrude","SWEPT_FACE",FACE,{"disambiguationData":[OSD([sQuery(id+"F0.wireOp",EDGE,"E1")])]});Q91=makeQuery(id+"F7.boolean.opBoolean","MERGE",FACE,{"derivedFrom":[subQ0,makeQuery(id+"F7.opPattern","COPY",FACE,{"derivedFrom":subQ0,"instanceName":"1"})]});}
            var Q92;
            Q92=makeQuery(id+"F7.opPattern","COPY",EDGE,{"derivedFrom":makeQuery(id+"F3.opExtrude","CAP_EDGE",EDGE,{"disambiguationData":[OSD([sQuery(id+"F2.wireOp",EDGE,"E18")])],"isStart":true}),"instanceName":"1"});
            var Q93;
            Q93=makeQuery(id+"F1.opExtrude","CAP_EDGE",EDGE,{"disambiguationData":[OSD([sQuery(id+"F0.wireOp",EDGE,"E6")])],"isStart":true});
            var Q94;
            Q94=makeQuery(id+"F7.opPattern","COPY",EDGE,{"derivedFrom":makeQuery(id+"F3.opExtrude","SWEPT_EDGE",EDGE,{"disambiguationData":[OSD([sQuery(id+"F2.wireOp",EDGE,"E16"),sQuery(id+"F2.wireOp",EDGE,"E17")])]}),"instanceName":"1"});
            var Q95;
            Q95=makeQuery(id+"F7.opPattern","COPY",EDGE,{"derivedFrom":makeQuery(id+"F3.opExtrude","SWEPT_EDGE",EDGE,{"disambiguationData":[OSD([sQuery(id+"F2.wireOp",EDGE,"E17"),sQuery(id+"F2.wireOp",EDGE,"E18")])]}),"instanceName":"1"});
            var Q96;
            {var subQ0=makeQuery(id+"F1.opExtrude","SWEPT_FACE",FACE,{"disambiguationData":[OSD([sQuery(id+"F0.wireOp",EDGE,"E0.right")])]});Q96=makeQuery(id+"F7.boolean.opBoolean","MERGE",FACE,{"derivedFrom":[subQ0,makeQuery(id+"F7.opPattern","COPY",FACE,{"derivedFrom":subQ0,"instanceName":"1"})]});}
            var Q97;
            {var subQ0=makeQuery(id+"F1.opExtrude","SWEPT_EDGE",EDGE,{"disambiguationData":[OSD([sQuery(id+"F0.wireOp",EDGE,"E3.3.3"),sQuery(id+"F0.wireOp",EDGE,"E10.trimOffspring")])]});Q97=makeQuery(id+"F7.boolean.opBoolean","MERGE",EDGE,{"derivedFrom":[subQ0,makeQuery(id+"F7.opPattern","COPY",EDGE,{"derivedFrom":subQ0,"instanceName":"1"})]});}
            var Q98;
            Q98=makeQuery(id+"F7.opPattern","COPY",EDGE,{"derivedFrom":makeQuery(id+"F3.opExtrude","SWEPT_EDGE",EDGE,{"disambiguationData":[OSD([sQuery(id+"F2.wireOp",EDGE,"E21"),sQuery(id+"F2.wireOp",EDGE,"E22")])]}),"instanceName":"1"});
            var Q99;
            Q99=makeQuery(id+"F7.opPattern","COPY",FACE,{"derivedFrom":makeQuery(id+"F6.opLoft","SWEPT_FACE",FACE,{"disambiguationData":[OSD([sQuery(id+"F2.wireOp",EDGE,"E16"),sQuery(id+"F2.wireOp",EDGE,"E17"),sQuery(id+"F2.wireOp",EDGE,"E18"),sQuery(id+"F4.wireOp",EDGE,"E26"),sQuery(id+"F4.wireOp",EDGE,"E27"),sQuery(id+"F4.wireOp",EDGE,"E32")])]}),"instanceName":"1"});
            var Q100;
            Q100=makeQuery(id+"F7.opPattern","COPY",EDGE,{"derivedFrom":makeQuery(id+"F3.opExtrude","CAP_EDGE",EDGE,{"disambiguationData":[OSD([sQuery(id+"F2.wireOp",EDGE,"E16")])],"isStart":true}),"instanceName":"1"});
            var Q101;
            Q101=makeQuery(id+"F7.boolean.opBoolean","INTERSECT",EDGE,{"derivedFrom":[makeQuery(id+"F7.opPattern","COPY",FACE,{"derivedFrom":makeQuery(id+"F1.opExtrude","SWEPT_FACE",FACE,{"disambiguationData":[OSD([sQuery(id+"F0.wireOp",EDGE,"E7")])]}),"instanceName":"1"}),makeQuery(id+"F7.opPattern","COPY",FACE,{"derivedFrom":makeQuery(id+"F6.opLoft","SWEPT_FACE",FACE,{"disambiguationData":[OSD([sQuery(id+"F2.wireOp",EDGE,"E15"),sQuery(id+"F2.wireOp",EDGE,"E16"),sQuery(id+"F2.wireOp",EDGE,"E17"),sQuery(id+"F4.wireOp",EDGE,"E25"),sQuery(id+"F4.wireOp",EDGE,"E26"),sQuery(id+"F4.wireOp",EDGE,"E27")])]}),"instanceName":"1"})]});
            var Q102;
            Q102=makeQuery(id+"F7.boolean.opBoolean","INTERSECT",EDGE,{"derivedFrom":[makeQuery(id+"F7.opPattern","COPY",FACE,{"derivedFrom":makeQuery(id+"F1.opExtrude","SWEPT_FACE",FACE,{"disambiguationData":[OSD([sQuery(id+"F0.wireOp",EDGE,"E8")])]}),"instanceName":"1"}),makeQuery(id+"F7.opPattern","COPY",FACE,{"derivedFrom":makeQuery(id+"F6.opLoft","SWEPT_FACE",FACE,{"disambiguationData":[OSD([sQuery(id+"F2.wireOp",EDGE,"E17"),sQuery(id+"F2.wireOp",EDGE,"E18"),sQuery(id+"F2.wireOp",EDGE,"E19"),sQuery(id+"F4.wireOp",EDGE,"E27"),sQuery(id+"F4.wireOp",EDGE,"E31"),sQuery(id+"F4.wireOp",EDGE,"E32")])]}),"instanceName":"1"})]});
            var Q103;
            {var subQ0=sQuery(id+"F2.wireOp",EDGE,"E16");Q103=makeQuery(id+"F7.boolean.opBoolean","MERGE",EDGE,{"derivedFrom":[makeQuery(id+"F7.opPattern","COPY",EDGE,{"derivedFrom":makeQuery(id+"F3.opExtrude","CAP_EDGE",EDGE,{"disambiguationData":[OSD([subQ0])],"isStart":false}),"instanceName":"1"}),makeQuery(id+"F7.opPattern","COPY",EDGE,{"derivedFrom":makeQuery(id+"F6.opLoft","MID_CAP_EDGE",EDGE,{"disambiguationData":[OSD([sQuery(id+"F2.wireOp",EDGE,"E15"),subQ0,sQuery(id+"F2.wireOp",EDGE,"E17")])],"capPos":0.0}),"instanceName":"1"})]});}
            var Q104;
            Q104=makeQuery(id+"F7.opPattern","COPY",FACE,{"derivedFrom":makeQuery(id+"F6.opLoft","SWEPT_FACE",FACE,{"disambiguationData":[OSD([sQuery(id+"F2.wireOp",EDGE,"E15"),sQuery(id+"F2.wireOp",EDGE,"E21"),sQuery(id+"F2.wireOp",EDGE,"E22"),sQuery(id+"F4.wireOp",EDGE,"E25"),sQuery(id+"F4.wireOp",EDGE,"E29"),sQuery(id+"F4.wireOp",EDGE,"E30")])]}),"instanceName":"1"});
            var Q105;
            {var subQ0=sQuery(id+"F2.wireOp",EDGE,"E17");Q105=makeQuery(id+"F7.boolean.opBoolean","MERGE",EDGE,{"derivedFrom":[makeQuery(id+"F7.opPattern","COPY",EDGE,{"derivedFrom":makeQuery(id+"F3.opExtrude","CAP_EDGE",EDGE,{"disambiguationData":[OSD([subQ0])],"isStart":false}),"instanceName":"1"}),makeQuery(id+"F7.opPattern","COPY",EDGE,{"derivedFrom":makeQuery(id+"F6.opLoft","MID_CAP_EDGE",EDGE,{"disambiguationData":[OSD([sQuery(id+"F2.wireOp",EDGE,"E16"),subQ0,sQuery(id+"F2.wireOp",EDGE,"E18")])],"capPos":0.0}),"instanceName":"1"})]});}
            var Q106;
            Q106=makeQuery(id+"F7.opPattern","COPY",FACE,{"derivedFrom":makeQuery(id+"F6.opLoft","SWEPT_FACE",FACE,{"disambiguationData":[OSD([sQuery(id+"F2.wireOp",EDGE,"E15"),sQuery(id+"F2.wireOp",EDGE,"E16"),sQuery(id+"F2.wireOp",EDGE,"E17"),sQuery(id+"F4.wireOp",EDGE,"E25"),sQuery(id+"F4.wireOp",EDGE,"E26"),sQuery(id+"F4.wireOp",EDGE,"E27")])]}),"instanceName":"1"});
            var Q107;
            {var subQ0=sQuery(id+"F2.wireOp",EDGE,"E18");Q107=makeQuery(id+"F7.boolean.opBoolean","MERGE",EDGE,{"derivedFrom":[makeQuery(id+"F7.opPattern","COPY",EDGE,{"derivedFrom":makeQuery(id+"F3.opExtrude","CAP_EDGE",EDGE,{"disambiguationData":[OSD([subQ0])],"isStart":false}),"instanceName":"1"}),makeQuery(id+"F7.opPattern","COPY",EDGE,{"derivedFrom":makeQuery(id+"F6.opLoft","MID_CAP_EDGE",EDGE,{"disambiguationData":[OSD([sQuery(id+"F2.wireOp",EDGE,"E17"),subQ0,sQuery(id+"F2.wireOp",EDGE,"E19")])],"capPos":0.0}),"instanceName":"1"})]});}
            var Q108;
            Q108=makeQuery(id+"F7.opPattern","COPY",FACE,{"derivedFrom":makeQuery(id+"F6.opLoft","SWEPT_FACE",FACE,{"disambiguationData":[OSD([sQuery(id+"F2.wireOp",EDGE,"E17"),sQuery(id+"F2.wireOp",EDGE,"E18"),sQuery(id+"F2.wireOp",EDGE,"E19"),sQuery(id+"F4.wireOp",EDGE,"E27"),sQuery(id+"F4.wireOp",EDGE,"E31"),sQuery(id+"F4.wireOp",EDGE,"E32")])]}),"instanceName":"1"});
            var Q109;
            {var subQ0=sQuery(id+"F2.wireOp",EDGE,"E19");Q109=makeQuery(id+"F7.boolean.opBoolean","MERGE",EDGE,{"derivedFrom":[makeQuery(id+"F7.opPattern","COPY",EDGE,{"derivedFrom":makeQuery(id+"F3.opExtrude","CAP_EDGE",EDGE,{"disambiguationData":[OSD([subQ0])],"isStart":false}),"instanceName":"1"}),makeQuery(id+"F7.opPattern","COPY",EDGE,{"derivedFrom":makeQuery(id+"F6.opLoft","MID_CAP_EDGE",EDGE,{"disambiguationData":[OSD([sQuery(id+"F2.wireOp",EDGE,"E18"),subQ0,sQuery(id+"F2.wireOp",EDGE,"E20")])],"capPos":0.0}),"instanceName":"1"})]});}
            var Q110;
            Q110=makeQuery(id+"F7.opPattern","COPY",FACE,{"derivedFrom":makeQuery(id+"F6.opLoft","SWEPT_FACE",FACE,{"disambiguationData":[OSD([sQuery(id+"F2.wireOp",EDGE,"E19"),sQuery(id+"F2.wireOp",EDGE,"E20"),sQuery(id+"F2.wireOp",EDGE,"E21"),sQuery(id+"F4.wireOp",EDGE,"E28"),sQuery(id+"F4.wireOp",EDGE,"E29"),sQuery(id+"F4.wireOp",EDGE,"E31")])]}),"instanceName":"1"});
            var Q111;
            {var subQ0=sQuery(id+"F2.wireOp",EDGE,"E21");Q111=makeQuery(id+"F7.boolean.opBoolean","MERGE",EDGE,{"derivedFrom":[makeQuery(id+"F7.opPattern","COPY",EDGE,{"derivedFrom":makeQuery(id+"F3.opExtrude","CAP_EDGE",EDGE,{"disambiguationData":[OSD([subQ0])],"isStart":false}),"instanceName":"1"}),makeQuery(id+"F7.opPattern","COPY",EDGE,{"derivedFrom":makeQuery(id+"F6.opLoft","MID_CAP_EDGE",EDGE,{"disambiguationData":[OSD([sQuery(id+"F2.wireOp",EDGE,"E20"),subQ0,sQuery(id+"F2.wireOp",EDGE,"E22")])],"capPos":0.0}),"instanceName":"1"})]});}
            var Q112;
            {var subQ0=sQuery(id+"F2.wireOp",EDGE,"E22");Q112=makeQuery(id+"F7.boolean.opBoolean","MERGE",EDGE,{"derivedFrom":[makeQuery(id+"F7.opPattern","COPY",EDGE,{"derivedFrom":makeQuery(id+"F3.opExtrude","CAP_EDGE",EDGE,{"disambiguationData":[OSD([subQ0])],"isStart":false}),"instanceName":"1"}),makeQuery(id+"F7.opPattern","COPY",EDGE,{"derivedFrom":makeQuery(id+"F6.opLoft","MID_CAP_EDGE",EDGE,{"disambiguationData":[OSD([sQuery(id+"F2.wireOp",EDGE,"E15"),sQuery(id+"F2.wireOp",EDGE,"E21"),subQ0])],"capPos":0.0}),"instanceName":"1"})]});}
            var Q113;
            {var subQ0=sQuery(id+"F4.wireOp",EDGE,"E25");Q113=makeQuery(id+"F7.boolean.opBoolean","MERGE",EDGE,{"derivedFrom":[makeQuery(id+"F7.opPattern","COPY",EDGE,{"derivedFrom":makeQuery(id+"F5.opExtrude","CAP_EDGE",EDGE,{"disambiguationData":[OSD([subQ0])],"isStart":false}),"instanceName":"1"}),makeQuery(id+"F7.opPattern","COPY",EDGE,{"derivedFrom":makeQuery(id+"F6.opLoft","MID_CAP_EDGE",EDGE,{"disambiguationData":[OSD([subQ0,sQuery(id+"F4.wireOp",EDGE,"E26"),sQuery(id+"F4.wireOp",EDGE,"E30")])],"capPos":1.0}),"instanceName":"1"})]});}
            var Q114;
            {var subQ0=sQuery(id+"F4.wireOp",EDGE,"E27");Q114=makeQuery(id+"F7.boolean.opBoolean","MERGE",EDGE,{"derivedFrom":[makeQuery(id+"F7.opPattern","COPY",EDGE,{"derivedFrom":makeQuery(id+"F5.opExtrude","CAP_EDGE",EDGE,{"disambiguationData":[OSD([subQ0])],"isStart":false}),"instanceName":"1"}),makeQuery(id+"F7.opPattern","COPY",EDGE,{"derivedFrom":makeQuery(id+"F6.opLoft","MID_CAP_EDGE",EDGE,{"disambiguationData":[OSD([sQuery(id+"F4.wireOp",EDGE,"E26"),subQ0,sQuery(id+"F4.wireOp",EDGE,"E32")])],"capPos":1.0}),"instanceName":"1"})]});}
            var Q115;
            {var subQ0=sQuery(id+"F4.wireOp",EDGE,"E31");var subQ1=sQuery(id+"F4.wireOp",EDGE,"E28");var subQ2=sQuery(id+"F2.wireOp",EDGE,"E20");var subQ3=sQuery(id+"F2.wireOp",EDGE,"E19");Q115=makeQuery(id+"F7.boolean.opBoolean","SPLIT",EDGE,{"disambiguationData":[topologyDisambiguationEdgeConnected([makeQuery(id+"F7.opPattern","COPY",FACE,{"derivedFrom":makeQuery(id+"F6.opLoft","SWEPT_FACE",FACE,{"disambiguationData":[OSD([subQ3,subQ2,sQuery(id+"F2.wireOp",EDGE,"E21"),subQ1,sQuery(id+"F4.wireOp",EDGE,"E29"),subQ0])]}),"instanceName":"1"})])],"derivedFrom":makeQuery(id+"F7.opPattern","COPY",EDGE,{"derivedFrom":makeQuery(id+"F6.opLoft","SWEPT_EDGE",EDGE,{"disambiguationData":[OSD([subQ3,subQ2,subQ1,subQ0])]}),"instanceName":"1"})});}
            var Q116;
            {var subQ0=sQuery(id+"F4.wireOp",EDGE,"E31");Q116=makeQuery(id+"F7.boolean.opBoolean","MERGE",EDGE,{"derivedFrom":[makeQuery(id+"F7.opPattern","COPY",EDGE,{"derivedFrom":makeQuery(id+"F5.opExtrude","CAP_EDGE",EDGE,{"disambiguationData":[OSD([subQ0])],"isStart":false}),"instanceName":"1"}),makeQuery(id+"F7.opPattern","COPY",EDGE,{"derivedFrom":makeQuery(id+"F6.opLoft","MID_CAP_EDGE",EDGE,{"disambiguationData":[OSD([sQuery(id+"F4.wireOp",EDGE,"E28"),subQ0,sQuery(id+"F4.wireOp",EDGE,"E32")])],"capPos":1.0}),"instanceName":"1"})]});}
            var Q117;
            Q117=makeQuery(id+"F6.opLoft","MID_CAP_EDGE",EDGE,{"disambiguationData":[OSD([sQuery(id+"F4.wireOp",EDGE,"E26"),sQuery(id+"F4.wireOp",EDGE,"E27"),sQuery(id+"F4.wireOp",EDGE,"E32")])],"capPos":1.0});
            var Q118;
            Q118=makeQuery(id+"F6.opLoft","SWEPT_EDGE",EDGE,{"disambiguationData":[OSD([sQuery(id+"F2.wireOp",EDGE,"E18"),sQuery(id+"F2.wireOp",EDGE,"E19"),sQuery(id+"F4.wireOp",EDGE,"E31"),sQuery(id+"F4.wireOp",EDGE,"E32")])]});
            var Q119;
            Q119=makeQuery(id+"F6.opLoft","CAP_FACE",FACE,{"disambiguationData":[OSD([sQuery(id+"F4.wireOp",EDGE,"E25"),sQuery(id+"F4.wireOp",EDGE,"E26"),sQuery(id+"F4.wireOp",EDGE,"E27"),sQuery(id+"F4.wireOp",EDGE,"E28"),sQuery(id+"F4.wireOp",EDGE,"E29"),sQuery(id+"F4.wireOp",EDGE,"E30"),sQuery(id+"F4.wireOp",EDGE,"E31"),sQuery(id+"F4.wireOp",EDGE,"E32")])],"isStart":true});
            var Q120;
            Q120=makeQuery(id+"F6.opLoft","SWEPT_FACE",FACE,{"disambiguationData":[OSD([sQuery(id+"F2.wireOp",EDGE,"E20"),sQuery(id+"F2.wireOp",EDGE,"E21"),sQuery(id+"F2.wireOp",EDGE,"E22"),sQuery(id+"F4.wireOp",EDGE,"E28"),sQuery(id+"F4.wireOp",EDGE,"E29"),sQuery(id+"F4.wireOp",EDGE,"E30")])]});
            var Q121;
            Q121=makeQuery(id+"F6.opLoft","SWEPT_EDGE",EDGE,{"disambiguationData":[OSD([sQuery(id+"F2.wireOp",EDGE,"E17"),sQuery(id+"F2.wireOp",EDGE,"E18"),sQuery(id+"F4.wireOp",EDGE,"E27"),sQuery(id+"F4.wireOp",EDGE,"E32")])]});
            var Q122;
            Q122=makeQuery(id+"F6.opLoft","SWEPT_FACE",FACE,{"disambiguationData":[OSD([sQuery(id+"F2.wireOp",EDGE,"E15"),sQuery(id+"F2.wireOp",EDGE,"E21"),sQuery(id+"F2.wireOp",EDGE,"E22"),sQuery(id+"F4.wireOp",EDGE,"E25"),sQuery(id+"F4.wireOp",EDGE,"E29"),sQuery(id+"F4.wireOp",EDGE,"E30")])]});
            var Q123;
            Q123=makeQuery(id+"F6.opLoft","SWEPT_EDGE",EDGE,{"disambiguationData":[OSD([sQuery(id+"F2.wireOp",EDGE,"E19"),sQuery(id+"F2.wireOp",EDGE,"E20"),sQuery(id+"F4.wireOp",EDGE,"E28"),sQuery(id+"F4.wireOp",EDGE,"E31")])]});
            var Q124;
            Q124=makeQuery(id+"F6.opLoft","SWEPT_FACE",FACE,{"disambiguationData":[OSD([sQuery(id+"F2.wireOp",EDGE,"E15"),sQuery(id+"F2.wireOp",EDGE,"E16"),sQuery(id+"F2.wireOp",EDGE,"E17"),sQuery(id+"F4.wireOp",EDGE,"E25"),sQuery(id+"F4.wireOp",EDGE,"E26"),sQuery(id+"F4.wireOp",EDGE,"E27")])]});
            var Q125;
            Q125=makeQuery(id+"F6.opLoft","SWEPT_EDGE",EDGE,{"disambiguationData":[OSD([sQuery(id+"F2.wireOp",EDGE,"E20"),sQuery(id+"F2.wireOp",EDGE,"E21"),sQuery(id+"F4.wireOp",EDGE,"E28"),sQuery(id+"F4.wireOp",EDGE,"E29")])]});
            var Q126;
            Q126=makeQuery(id+"F6.opLoft","MID_CAP_EDGE",EDGE,{"disambiguationData":[OSD([sQuery(id+"F2.wireOp",EDGE,"E16"),sQuery(id+"F2.wireOp",EDGE,"E17"),sQuery(id+"F2.wireOp",EDGE,"E18")])],"capPos":0.0});
            var Q127;
            Q127=makeQuery(id+"F5.opExtrude","CAP_EDGE",EDGE,{"disambiguationData":[OSD([sQuery(id+"F4.wireOp",EDGE,"E30")])],"isStart":true});
            var Q128;
            Q128=makeQuery(id+"F5.opExtrude","SWEPT_EDGE",EDGE,{"disambiguationData":[OSD([sQuery(id+"F4.wireOp",EDGE,"E29"),sQuery(id+"F4.wireOp",EDGE,"E30")])]});
            var Q129;
            Q129=makeQuery(id+"F5.opExtrude","CAP_EDGE",EDGE,{"disambiguationData":[OSD([sQuery(id+"F4.wireOp",EDGE,"E28")])],"isStart":false});
            var Q130;
            Q130=makeQuery(id+"F5.opExtrude","CAP_EDGE",EDGE,{"disambiguationData":[OSD([sQuery(id+"F4.wireOp",EDGE,"E32")])],"isStart":false});
            var Q131;
            Q131=makeQuery(id+"F5.opExtrude","CAP_EDGE",EDGE,{"disambiguationData":[OSD([sQuery(id+"F4.wireOp",EDGE,"E30")])],"isStart":false});
            var Q132;
            Q132=makeQuery(id+"F5.opExtrude","SWEPT_EDGE",EDGE,{"disambiguationData":[OSD([sQuery(id+"F4.wireOp",EDGE,"E31"),sQuery(id+"F4.wireOp",EDGE,"E32")])]});
            var Q133;
            Q133=makeQuery(id+"F5.opExtrude","SWEPT_EDGE",EDGE,{"disambiguationData":[OSD([sQuery(id+"F4.wireOp",EDGE,"E27"),sQuery(id+"F4.wireOp",EDGE,"E32")])]});
            var Q134;
            Q134=makeQuery(id+"F5.opExtrude","SWEPT_EDGE",EDGE,{"disambiguationData":[OSD([sQuery(id+"F4.wireOp",EDGE,"E25"),sQuery(id+"F4.wireOp",EDGE,"E26")])]});
            var Q135;
            Q135=makeQuery(id+"F5.opExtrude","SWEPT_EDGE",EDGE,{"disambiguationData":[OSD([sQuery(id+"F4.wireOp",EDGE,"E25"),sQuery(id+"F4.wireOp",EDGE,"E30")])]});
            var Q136;
            Q136=makeQuery(id+"F3.opExtrude","SWEPT_EDGE",EDGE,{"disambiguationData":[OSD([sQuery(id+"F2.wireOp",EDGE,"E15"),sQuery(id+"F2.wireOp",EDGE,"E16")])]});
            var Q137;
            Q137=makeQuery(id+"F3.opExtrude","SWEPT_EDGE",EDGE,{"disambiguationData":[OSD([sQuery(id+"F2.wireOp",EDGE,"E17"),sQuery(id+"F2.wireOp",EDGE,"E18")])]});
            var Q138;
            Q138=makeQuery(id+"F3.opExtrude","CAP_EDGE",EDGE,{"disambiguationData":[OSD([sQuery(id+"F2.wireOp",EDGE,"E16")])],"isStart":false});
            var Q139;
            Q139=makeQuery(id+"F3.opExtrude","SWEPT_EDGE",EDGE,{"disambiguationData":[OSD([sQuery(id+"F2.wireOp",EDGE,"E18"),sQuery(id+"F2.wireOp",EDGE,"E19")])]});
            var Q140;
            Q140=makeQuery(id+"F3.opExtrude","CAP_EDGE",EDGE,{"disambiguationData":[OSD([sQuery(id+"F2.wireOp",EDGE,"E20")])],"isStart":false});
            var Q141;
            Q141=makeQuery(id+"F3.opExtrude","SWEPT_FACE",FACE,{"disambiguationData":[OSD([sQuery(id+"F2.wireOp",EDGE,"E22")])]});
            var Q142;
            Q142=makeQuery(id+"F3.opExtrude","CAP_EDGE",EDGE,{"disambiguationData":[OSD([sQuery(id+"F2.wireOp",EDGE,"E21")])],"isStart":false});
            var Q143;
            Q143=makeQuery(id+"F3.opExtrude","CAP_EDGE",EDGE,{"disambiguationData":[OSD([sQuery(id+"F2.wireOp",EDGE,"E21")])],"isStart":true});
            var Q144;
            Q144=makeQuery(id+"F3.opExtrude","CAP_EDGE",EDGE,{"disambiguationData":[OSD([sQuery(id+"F2.wireOp",EDGE,"E20")])],"isStart":true});
            var Q145;
            Q145=makeQuery(id+"F3.opExtrude","SWEPT_EDGE",EDGE,{"disambiguationData":[OSD([sQuery(id+"F2.wireOp",EDGE,"E20"),sQuery(id+"F2.wireOp",EDGE,"E21")])]});
            var Q146;
            Q146=makeQuery(id+"F3.opExtrude","SWEPT_FACE",FACE,{"disambiguationData":[OSD([sQuery(id+"F2.wireOp",EDGE,"E15")])]});
            var Q147;
            Q147=makeQuery(id+"F1.opExtrude","CAP_EDGE",EDGE,{"disambiguationData":[OSD([sQuery(id+"F0.wireOp",EDGE,"E0.right")])],"isStart":true});
            var Q148;
            Q148=makeQuery(id+"F1.opExtrude","CAP_EDGE",EDGE,{"disambiguationData":[OSD([sQuery(id+"F0.wireOp",EDGE,"E0.left")])],"isStart":true});
            var Q149;
            Q149=makeQuery(id+"F1.opExtrude","CAP_EDGE",EDGE,{"disambiguationData":[OSD([sQuery(id+"F0.wireOp",EDGE,"E3.1.0")])],"isStart":true});
            var Q150;
            Q150=makeQuery(id+"F1.opExtrude","CAP_EDGE",EDGE,{"disambiguationData":[OSD([sQuery(id+"F0.wireOp",EDGE,"E9.trimOffspring")])],"isStart":true});
            var Q151;
            {var subQ0=makeQuery(id+"F1.opExtrude","SWEPT_EDGE",EDGE,{"disambiguationData":[OSD([sQuery(id+"F0.wireOp",EDGE,"E2"),sQuery(id+"F0.wireOp",EDGE,"E4")])]});Q151=makeQuery(id+"F7.boolean.opBoolean","MERGE",EDGE,{"derivedFrom":[subQ0,makeQuery(id+"F7.opPattern","COPY",EDGE,{"derivedFrom":subQ0,"instanceName":"1"})]});}
            var Q152;
            Q152=makeQuery(id+"F1.opExtrude","CAP_EDGE",EDGE,{"disambiguationData":[OSD([sQuery(id+"F0.wireOp",EDGE,"E3.2.3")])],"isStart":true});
            var Q153;
            Q153=makeQuery(id+"F1.opExtrude","CAP_EDGE",EDGE,{"disambiguationData":[OSD([sQuery(id+"F0.wireOp",EDGE,"E10.trimOffspring")])],"isStart":true});
            var Q154;
            Q154=makeQuery(id+"F1.opExtrude","CAP_EDGE",EDGE,{"disambiguationData":[OSD([sQuery(id+"F0.wireOp",EDGE,"E8")])],"isStart":true});
            var Q155;
            Q155=makeQuery(id+"F1.opExtrude","CAP_EDGE",EDGE,{"disambiguationData":[OSD([sQuery(id+"F0.wireOp",EDGE,"E3.1.3")])],"isStart":true});
            var Q156;
            Q156=makeQuery(id+"F1.opExtrude","CAP_EDGE",EDGE,{"disambiguationData":[OSD([sQuery(id+"F0.wireOp",EDGE,"E3.2.0")])],"isStart":true});
            var Q157;
            Q157=makeQuery(id+"F7.boolean.opBoolean","INTERSECT",EDGE,{"derivedFrom":[makeQuery(id+"F7.opPattern","COPY",FACE,{"derivedFrom":makeQuery(id+"F1.opExtrude","SWEPT_FACE",FACE,{"disambiguationData":[OSD([sQuery(id+"F0.wireOp",EDGE,"E6")])]}),"instanceName":"1"}),makeQuery(id+"F7.opPattern","COPY",FACE,{"derivedFrom":makeQuery(id+"F6.opLoft","SWEPT_FACE",FACE,{"disambiguationData":[OSD([sQuery(id+"F2.wireOp",EDGE,"E19"),sQuery(id+"F2.wireOp",EDGE,"E20"),sQuery(id+"F2.wireOp",EDGE,"E21"),sQuery(id+"F4.wireOp",EDGE,"E28"),sQuery(id+"F4.wireOp",EDGE,"E29"),sQuery(id+"F4.wireOp",EDGE,"E31")])]}),"instanceName":"1"})]});
            var Q158;
            {var subQ0=makeQuery(id+"F1.opExtrude","SWEPT_FACE",FACE,{"disambiguationData":[OSD([sQuery(id+"F0.wireOp",EDGE,"E3.1.0")])]});var subQ1=sQuery(id+"F4.wireOp",EDGE,"E29");var subQ2=sQuery(id+"F4.wireOp",EDGE,"E28");var subQ3=sQuery(id+"F2.wireOp",EDGE,"E21");var subQ4=sQuery(id+"F2.wireOp",EDGE,"E20");Q158=makeQuery(id+"F7.boolean.opBoolean","SPLIT",EDGE,{"disambiguationData":[topologyDisambiguationEdgeConnected([subQ0])],"derivedFrom":makeQuery(id+"F7.opPattern","COPY",EDGE,{"derivedFrom":makeQuery(id+"F6.opLoft","SWEPT_EDGE",EDGE,{"disambiguationData":[OSD([subQ4,subQ3,subQ2,subQ1])]}),"instanceName":"1"})});}
            var Q159;
            {var subQ0=sQuery(id+"F4.wireOp",EDGE,"E30");var subQ1=sQuery(id+"F4.wireOp",EDGE,"E29");var subQ2=sQuery(id+"F2.wireOp",EDGE,"E22");var subQ3=sQuery(id+"F2.wireOp",EDGE,"E21");Q159=makeQuery(id+"F7.boolean.opBoolean","SPLIT",EDGE,{"disambiguationData":[topologyDisambiguationEdgeConnected([makeQuery(id+"F7.opPattern","COPY",FACE,{"derivedFrom":makeQuery(id+"F6.opLoft","SWEPT_FACE",FACE,{"disambiguationData":[OSD([sQuery(id+"F2.wireOp",EDGE,"E15"),subQ3,subQ2,sQuery(id+"F4.wireOp",EDGE,"E25"),subQ1,subQ0])]}),"instanceName":"1"})])],"derivedFrom":makeQuery(id+"F7.opPattern","COPY",EDGE,{"derivedFrom":makeQuery(id+"F6.opLoft","SWEPT_EDGE",EDGE,{"disambiguationData":[OSD([subQ3,subQ2,subQ1,subQ0])]}),"instanceName":"1"})});}
            var Q160;
            {var subQ0=makeQuery(id+"F1.opExtrude","SWEPT_FACE",FACE,{"disambiguationData":[OSD([sQuery(id+"F0.wireOp",EDGE,"E2")])]});var subQ1=sQuery(id+"F4.wireOp",EDGE,"E30");var subQ2=sQuery(id+"F4.wireOp",EDGE,"E29");var subQ3=sQuery(id+"F2.wireOp",EDGE,"E22");var subQ4=sQuery(id+"F2.wireOp",EDGE,"E21");Q160=makeQuery(id+"F7.boolean.opBoolean","SPLIT",EDGE,{"disambiguationData":[topologyDisambiguationEdgeConnected([subQ0])],"derivedFrom":makeQuery(id+"F7.opPattern","COPY",EDGE,{"derivedFrom":makeQuery(id+"F6.opLoft","SWEPT_EDGE",EDGE,{"disambiguationData":[OSD([subQ4,subQ3,subQ2,subQ1])]}),"instanceName":"1"})});}
            var Q161;
            {var subQ0=sQuery(id+"F2.wireOp",EDGE,"E15");Q161=makeQuery(id+"F7.boolean.opBoolean","MERGE",EDGE,{"derivedFrom":[makeQuery(id+"F7.opPattern","COPY",EDGE,{"derivedFrom":makeQuery(id+"F3.opExtrude","CAP_EDGE",EDGE,{"disambiguationData":[OSD([subQ0])],"isStart":false}),"instanceName":"1"}),makeQuery(id+"F7.opPattern","COPY",EDGE,{"derivedFrom":makeQuery(id+"F6.opLoft","MID_CAP_EDGE",EDGE,{"disambiguationData":[OSD([subQ0,sQuery(id+"F2.wireOp",EDGE,"E16"),sQuery(id+"F2.wireOp",EDGE,"E22")])],"capPos":0.0}),"instanceName":"1"})]});}
            var Q162;
            {var subQ0=sQuery(id+"F4.wireOp",EDGE,"E30");var subQ1=sQuery(id+"F4.wireOp",EDGE,"E25");var subQ2=sQuery(id+"F2.wireOp",EDGE,"E22");var subQ3=sQuery(id+"F2.wireOp",EDGE,"E15");Q162=makeQuery(id+"F7.boolean.opBoolean","SPLIT",EDGE,{"disambiguationData":[topologyDisambiguationEdgeConnected([makeQuery(id+"F7.opPattern","COPY",FACE,{"derivedFrom":makeQuery(id+"F6.opLoft","SWEPT_FACE",FACE,{"disambiguationData":[OSD([subQ3,sQuery(id+"F2.wireOp",EDGE,"E21"),subQ2,subQ1,sQuery(id+"F4.wireOp",EDGE,"E29"),subQ0])]}),"instanceName":"1"})])],"derivedFrom":makeQuery(id+"F7.opPattern","COPY",EDGE,{"derivedFrom":makeQuery(id+"F6.opLoft","SWEPT_EDGE",EDGE,{"disambiguationData":[OSD([subQ3,subQ2,subQ1,subQ0])]}),"instanceName":"1"})});}
            var Q163;
            {var subQ0=makeQuery(id+"F1.opExtrude","SWEPT_FACE",FACE,{"disambiguationData":[OSD([sQuery(id+"F0.wireOp",EDGE,"E1")])]});var subQ1=sQuery(id+"F4.wireOp",EDGE,"E30");var subQ2=sQuery(id+"F4.wireOp",EDGE,"E25");var subQ3=sQuery(id+"F2.wireOp",EDGE,"E22");var subQ4=sQuery(id+"F2.wireOp",EDGE,"E15");Q163=makeQuery(id+"F7.boolean.opBoolean","SPLIT",EDGE,{"disambiguationData":[topologyDisambiguationEdgeConnected([subQ0])],"derivedFrom":makeQuery(id+"F7.opPattern","COPY",EDGE,{"derivedFrom":makeQuery(id+"F6.opLoft","SWEPT_EDGE",EDGE,{"disambiguationData":[OSD([subQ4,subQ3,subQ2,subQ1])]}),"instanceName":"1"})});}
            var Q164;
            {var subQ0=sQuery(id+"F4.wireOp",EDGE,"E26");var subQ1=sQuery(id+"F4.wireOp",EDGE,"E25");var subQ2=sQuery(id+"F2.wireOp",EDGE,"E16");var subQ3=sQuery(id+"F2.wireOp",EDGE,"E15");Q164=makeQuery(id+"F7.boolean.opBoolean","SPLIT",EDGE,{"disambiguationData":[topologyDisambiguationEdgeConnected([makeQuery(id+"F7.opPattern","COPY",FACE,{"derivedFrom":makeQuery(id+"F6.opLoft","SWEPT_FACE",FACE,{"disambiguationData":[OSD([subQ3,subQ2,sQuery(id+"F2.wireOp",EDGE,"E17"),subQ1,subQ0,sQuery(id+"F4.wireOp",EDGE,"E27")])]}),"instanceName":"1"})])],"derivedFrom":makeQuery(id+"F7.opPattern","COPY",EDGE,{"derivedFrom":makeQuery(id+"F6.opLoft","SWEPT_EDGE",EDGE,{"disambiguationData":[OSD([subQ3,subQ2,subQ1,subQ0])]}),"instanceName":"1"})});}
            var Q165;
            {var subQ0=makeQuery(id+"F1.opExtrude","SWEPT_FACE",FACE,{"disambiguationData":[OSD([sQuery(id+"F0.wireOp",EDGE,"E3.3.3")])]});var subQ1=sQuery(id+"F4.wireOp",EDGE,"E26");var subQ2=sQuery(id+"F4.wireOp",EDGE,"E25");var subQ3=sQuery(id+"F2.wireOp",EDGE,"E16");var subQ4=sQuery(id+"F2.wireOp",EDGE,"E15");Q165=makeQuery(id+"F7.boolean.opBoolean","SPLIT",EDGE,{"disambiguationData":[topologyDisambiguationEdgeConnected([subQ0])],"derivedFrom":makeQuery(id+"F7.opPattern","COPY",EDGE,{"derivedFrom":makeQuery(id+"F6.opLoft","SWEPT_EDGE",EDGE,{"disambiguationData":[OSD([subQ4,subQ3,subQ2,subQ1])]}),"instanceName":"1"})});}
            var Q166;
            {var subQ0=sQuery(id+"F4.wireOp",EDGE,"E27");var subQ1=sQuery(id+"F4.wireOp",EDGE,"E26");var subQ2=sQuery(id+"F2.wireOp",EDGE,"E17");var subQ3=sQuery(id+"F2.wireOp",EDGE,"E16");Q166=makeQuery(id+"F7.boolean.opBoolean","SPLIT",EDGE,{"disambiguationData":[topologyDisambiguationEdgeConnected([makeQuery(id+"F7.opPattern","COPY",FACE,{"derivedFrom":makeQuery(id+"F6.opLoft","SWEPT_FACE",FACE,{"disambiguationData":[OSD([sQuery(id+"F2.wireOp",EDGE,"E15"),subQ3,subQ2,sQuery(id+"F4.wireOp",EDGE,"E25"),subQ1,subQ0])]}),"instanceName":"1"})])],"derivedFrom":makeQuery(id+"F7.opPattern","COPY",EDGE,{"derivedFrom":makeQuery(id+"F6.opLoft","SWEPT_EDGE",EDGE,{"disambiguationData":[OSD([subQ3,subQ2,subQ1,subQ0])]}),"instanceName":"1"})});}
            var Q167;
            {var subQ0=sQuery(id+"F2.wireOp",EDGE,"E20");Q167=makeQuery(id+"F7.boolean.opBoolean","MERGE",EDGE,{"derivedFrom":[makeQuery(id+"F7.opPattern","COPY",EDGE,{"derivedFrom":makeQuery(id+"F3.opExtrude","CAP_EDGE",EDGE,{"disambiguationData":[OSD([subQ0])],"isStart":false}),"instanceName":"1"}),makeQuery(id+"F7.opPattern","COPY",EDGE,{"derivedFrom":makeQuery(id+"F6.opLoft","MID_CAP_EDGE",EDGE,{"disambiguationData":[OSD([sQuery(id+"F2.wireOp",EDGE,"E19"),subQ0,sQuery(id+"F2.wireOp",EDGE,"E21")])],"capPos":0.0}),"instanceName":"1"})]});}
            var Q168;
            {var subQ0=makeQuery(id+"F1.opExtrude","SWEPT_FACE",FACE,{"disambiguationData":[OSD([sQuery(id+"F0.wireOp",EDGE,"E3.3.0")])]});var subQ1=sQuery(id+"F4.wireOp",EDGE,"E27");var subQ2=sQuery(id+"F4.wireOp",EDGE,"E26");var subQ3=sQuery(id+"F2.wireOp",EDGE,"E17");var subQ4=sQuery(id+"F2.wireOp",EDGE,"E16");Q168=makeQuery(id+"F7.boolean.opBoolean","SPLIT",EDGE,{"disambiguationData":[topologyDisambiguationEdgeConnected([subQ0])],"derivedFrom":makeQuery(id+"F7.opPattern","COPY",EDGE,{"derivedFrom":makeQuery(id+"F6.opLoft","SWEPT_EDGE",EDGE,{"disambiguationData":[OSD([subQ4,subQ3,subQ2,subQ1])]}),"instanceName":"1"})});}
            var Q169;
            {var subQ0=sQuery(id+"F4.wireOp",EDGE,"E32");var subQ1=sQuery(id+"F4.wireOp",EDGE,"E27");var subQ2=sQuery(id+"F2.wireOp",EDGE,"E18");var subQ3=sQuery(id+"F2.wireOp",EDGE,"E17");Q169=makeQuery(id+"F7.boolean.opBoolean","SPLIT",EDGE,{"disambiguationData":[topologyDisambiguationEdgeConnected([makeQuery(id+"F7.opPattern","COPY",FACE,{"derivedFrom":makeQuery(id+"F6.opLoft","SWEPT_FACE",FACE,{"disambiguationData":[OSD([subQ3,subQ2,sQuery(id+"F2.wireOp",EDGE,"E19"),subQ1,sQuery(id+"F4.wireOp",EDGE,"E31"),subQ0])]}),"instanceName":"1"})])],"derivedFrom":makeQuery(id+"F7.opPattern","COPY",EDGE,{"derivedFrom":makeQuery(id+"F6.opLoft","SWEPT_EDGE",EDGE,{"disambiguationData":[OSD([subQ3,subQ2,subQ1,subQ0])]}),"instanceName":"1"})});}
            var Q170;
            {var subQ0=makeQuery(id+"F1.opExtrude","SWEPT_FACE",FACE,{"disambiguationData":[OSD([sQuery(id+"F0.wireOp",EDGE,"E3.2.3")])]});var subQ1=sQuery(id+"F4.wireOp",EDGE,"E32");var subQ2=sQuery(id+"F4.wireOp",EDGE,"E27");var subQ3=sQuery(id+"F2.wireOp",EDGE,"E18");var subQ4=sQuery(id+"F2.wireOp",EDGE,"E17");Q170=makeQuery(id+"F7.boolean.opBoolean","SPLIT",EDGE,{"disambiguationData":[topologyDisambiguationEdgeConnected([subQ0])],"derivedFrom":makeQuery(id+"F7.opPattern","COPY",EDGE,{"derivedFrom":makeQuery(id+"F6.opLoft","SWEPT_EDGE",EDGE,{"disambiguationData":[OSD([subQ4,subQ3,subQ2,subQ1])]}),"instanceName":"1"})});}
            var Q171;
            {var subQ0=sQuery(id+"F4.wireOp",EDGE,"E32");var subQ1=sQuery(id+"F4.wireOp",EDGE,"E31");var subQ2=sQuery(id+"F2.wireOp",EDGE,"E19");var subQ3=sQuery(id+"F2.wireOp",EDGE,"E18");Q171=makeQuery(id+"F7.boolean.opBoolean","SPLIT",EDGE,{"disambiguationData":[topologyDisambiguationEdgeConnected([makeQuery(id+"F7.opPattern","COPY",FACE,{"derivedFrom":makeQuery(id+"F6.opLoft","SWEPT_FACE",FACE,{"disambiguationData":[OSD([sQuery(id+"F2.wireOp",EDGE,"E17"),subQ3,subQ2,sQuery(id+"F4.wireOp",EDGE,"E27"),subQ1,subQ0])]}),"instanceName":"1"})])],"derivedFrom":makeQuery(id+"F7.opPattern","COPY",EDGE,{"derivedFrom":makeQuery(id+"F6.opLoft","SWEPT_EDGE",EDGE,{"disambiguationData":[OSD([subQ3,subQ2,subQ1,subQ0])]}),"instanceName":"1"})});}
            var Q172;
            {var subQ0=sQuery(id+"F4.wireOp",EDGE,"E29");Q172=makeQuery(id+"F7.boolean.opBoolean","MERGE",EDGE,{"derivedFrom":[makeQuery(id+"F7.opPattern","COPY",EDGE,{"derivedFrom":makeQuery(id+"F5.opExtrude","CAP_EDGE",EDGE,{"disambiguationData":[OSD([subQ0])],"isStart":false}),"instanceName":"1"}),makeQuery(id+"F7.opPattern","COPY",EDGE,{"derivedFrom":makeQuery(id+"F6.opLoft","MID_CAP_EDGE",EDGE,{"disambiguationData":[OSD([sQuery(id+"F4.wireOp",EDGE,"E28"),subQ0,sQuery(id+"F4.wireOp",EDGE,"E30")])],"capPos":1.0}),"instanceName":"1"})]});}
            var Q173;
            {var subQ0=makeQuery(id+"F1.opExtrude","SWEPT_FACE",FACE,{"disambiguationData":[OSD([sQuery(id+"F0.wireOp",EDGE,"E3.1.3")])]});var subQ1=sQuery(id+"F4.wireOp",EDGE,"E31");var subQ2=sQuery(id+"F4.wireOp",EDGE,"E28");var subQ3=sQuery(id+"F2.wireOp",EDGE,"E20");var subQ4=sQuery(id+"F2.wireOp",EDGE,"E19");Q173=makeQuery(id+"F7.boolean.opBoolean","SPLIT",EDGE,{"disambiguationData":[topologyDisambiguationEdgeConnected([subQ0])],"derivedFrom":makeQuery(id+"F7.opPattern","COPY",EDGE,{"derivedFrom":makeQuery(id+"F6.opLoft","SWEPT_EDGE",EDGE,{"disambiguationData":[OSD([subQ4,subQ3,subQ2,subQ1])]}),"instanceName":"1"})});}
            var Q174;
            Q174=makeQuery(id+"F7.boolean.opBoolean","INTERSECT",EDGE,{"derivedFrom":[makeQuery(id+"F7.opPattern","COPY",FACE,{"derivedFrom":makeQuery(id+"F1.opExtrude","SWEPT_FACE",FACE,{"disambiguationData":[OSD([sQuery(id+"F0.wireOp",EDGE,"E4")])]}),"instanceName":"1"}),makeQuery(id+"F7.opPattern","COPY",FACE,{"derivedFrom":makeQuery(id+"F6.opLoft","SWEPT_FACE",FACE,{"disambiguationData":[OSD([sQuery(id+"F2.wireOp",EDGE,"E15"),sQuery(id+"F2.wireOp",EDGE,"E21"),sQuery(id+"F2.wireOp",EDGE,"E22"),sQuery(id+"F4.wireOp",EDGE,"E25"),sQuery(id+"F4.wireOp",EDGE,"E29"),sQuery(id+"F4.wireOp",EDGE,"E30")])]}),"instanceName":"1"})]});
            var Q175;
            {var subQ0=sQuery(id+"F4.wireOp",EDGE,"E29");var subQ1=sQuery(id+"F4.wireOp",EDGE,"E28");var subQ2=sQuery(id+"F2.wireOp",EDGE,"E21");var subQ3=sQuery(id+"F2.wireOp",EDGE,"E20");Q175=makeQuery(id+"F7.boolean.opBoolean","SPLIT",EDGE,{"disambiguationData":[topologyDisambiguationEdgeConnected([makeQuery(id+"F7.opPattern","COPY",FACE,{"derivedFrom":makeQuery(id+"F6.opLoft","SWEPT_FACE",FACE,{"disambiguationData":[OSD([sQuery(id+"F2.wireOp",EDGE,"E19"),subQ3,subQ2,subQ1,subQ0,sQuery(id+"F4.wireOp",EDGE,"E31")])]}),"instanceName":"1"})])],"derivedFrom":makeQuery(id+"F7.opPattern","COPY",EDGE,{"derivedFrom":makeQuery(id+"F6.opLoft","SWEPT_EDGE",EDGE,{"disambiguationData":[OSD([subQ3,subQ2,subQ1,subQ0])]}),"instanceName":"1"})});}
            var Q176;
            Q176=makeQuery(id+"F6.opLoft","SWEPT_FACE",FACE,{"disambiguationData":[OSD([sQuery(id+"F2.wireOp",EDGE,"E15"),sQuery(id+"F2.wireOp",EDGE,"E16"),sQuery(id+"F2.wireOp",EDGE,"E22"),sQuery(id+"F4.wireOp",EDGE,"E25"),sQuery(id+"F4.wireOp",EDGE,"E26"),sQuery(id+"F4.wireOp",EDGE,"E30")])]});
            var Q177;
            Q177=makeQuery(id+"F6.opLoft","MID_CAP_EDGE",EDGE,{"disambiguationData":[OSD([sQuery(id+"F4.wireOp",EDGE,"E28"),sQuery(id+"F4.wireOp",EDGE,"E31"),sQuery(id+"F4.wireOp",EDGE,"E32")])],"capPos":1.0});
            var Q178;
            Q178=makeQuery(id+"F6.opLoft","MID_CAP_EDGE",EDGE,{"disambiguationData":[OSD([sQuery(id+"F2.wireOp",EDGE,"E17"),sQuery(id+"F2.wireOp",EDGE,"E18"),sQuery(id+"F2.wireOp",EDGE,"E19")])],"capPos":0.0});
            var Q179;
            Q179=makeQuery(id+"F6.opLoft","SWEPT_EDGE",EDGE,{"disambiguationData":[OSD([sQuery(id+"F2.wireOp",EDGE,"E16"),sQuery(id+"F2.wireOp",EDGE,"E17"),sQuery(id+"F4.wireOp",EDGE,"E26"),sQuery(id+"F4.wireOp",EDGE,"E27")])]});
            var Q180;
            Q180=makeQuery(id+"F6.opLoft","MID_CAP_EDGE",EDGE,{"disambiguationData":[OSD([sQuery(id+"F4.wireOp",EDGE,"E28"),sQuery(id+"F4.wireOp",EDGE,"E29"),sQuery(id+"F4.wireOp",EDGE,"E30")])],"capPos":1.0});
            var Q181;
            Q181=makeQuery(id+"F6.opLoft","MID_CAP_EDGE",EDGE,{"disambiguationData":[OSD([sQuery(id+"F2.wireOp",EDGE,"E18"),sQuery(id+"F2.wireOp",EDGE,"E19"),sQuery(id+"F2.wireOp",EDGE,"E20")])],"capPos":0.0});
            var Q182;
            Q182=makeQuery(id+"F6.opLoft","SWEPT_EDGE",EDGE,{"disambiguationData":[OSD([sQuery(id+"F2.wireOp",EDGE,"E15"),sQuery(id+"F2.wireOp",EDGE,"E16"),sQuery(id+"F4.wireOp",EDGE,"E25"),sQuery(id+"F4.wireOp",EDGE,"E26")])]});
            var Q183;
            Q183=makeQuery(id+"F6.opLoft","MID_CAP_EDGE",EDGE,{"disambiguationData":[OSD([sQuery(id+"F4.wireOp",EDGE,"E25"),sQuery(id+"F4.wireOp",EDGE,"E26"),sQuery(id+"F4.wireOp",EDGE,"E27")])],"capPos":1.0});
            var Q184;
            Q184=makeQuery(id+"F5.opExtrude","CAP_EDGE",EDGE,{"disambiguationData":[OSD([sQuery(id+"F4.wireOp",EDGE,"E25")])],"isStart":false});
            var Q185;
            Q185=makeQuery(id+"F5.opExtrude","CAP_EDGE",EDGE,{"disambiguationData":[OSD([sQuery(id+"F4.wireOp",EDGE,"E25")])],"isStart":true});
            var Q186;
            Q186=makeQuery(id+"F5.opExtrude","CAP_EDGE",EDGE,{"disambiguationData":[OSD([sQuery(id+"F4.wireOp",EDGE,"E28")])],"isStart":true});
            var Q187;
            Q187=makeQuery(id+"F5.opExtrude","CAP_EDGE",EDGE,{"disambiguationData":[OSD([sQuery(id+"F4.wireOp",EDGE,"E31")])],"isStart":true});
            var Q188;
            Q188=makeQuery(id+"F5.opExtrude","CAP_EDGE",EDGE,{"disambiguationData":[OSD([sQuery(id+"F4.wireOp",EDGE,"E32")])],"isStart":true});
            var Q189;
            Q189=makeQuery(id+"F5.opExtrude","CAP_EDGE",EDGE,{"disambiguationData":[OSD([sQuery(id+"F4.wireOp",EDGE,"E26")])],"isStart":true});
            var Q190;
            Q190=makeQuery(id+"F5.opExtrude","CAP_EDGE",EDGE,{"disambiguationData":[OSD([sQuery(id+"F4.wireOp",EDGE,"E27")])],"isStart":true});
            var Q191;
            Q191=makeQuery(id+"F5.opExtrude","CAP_EDGE",EDGE,{"disambiguationData":[OSD([sQuery(id+"F4.wireOp",EDGE,"E29")])],"isStart":true});
            var Q192;
            Q192=makeQuery(id+"F3.opExtrude","CAP_EDGE",EDGE,{"disambiguationData":[OSD([sQuery(id+"F2.wireOp",EDGE,"E22")])],"isStart":false});
            var Q193;
            Q193=makeQuery(id+"F3.opExtrude","CAP_EDGE",EDGE,{"disambiguationData":[OSD([sQuery(id+"F2.wireOp",EDGE,"E15")])],"isStart":true});
            var Q194;
            Q194=makeQuery(id+"F3.opExtrude","CAP_EDGE",EDGE,{"disambiguationData":[OSD([sQuery(id+"F2.wireOp",EDGE,"E15")])],"isStart":false});
            var Q195;
            Q195=makeQuery(id+"F3.opExtrude","CAP_EDGE",EDGE,{"disambiguationData":[OSD([sQuery(id+"F2.wireOp",EDGE,"E22")])],"isStart":true});
            var Q196;
            Q196=makeQuery(id+"F1.opExtrude","CAP_EDGE",EDGE,{"disambiguationData":[OSD([sQuery(id+"F0.wireOp",EDGE,"E7")])],"isStart":true});
            var Q197;
            Q197=makeQuery(id+"F1.opExtrude","CAP_EDGE",EDGE,{"disambiguationData":[OSD([sQuery(id+"F0.wireOp",EDGE,"E3.3.0")])],"isStart":true});
            var Q198;
            Q198=makeQuery(id+"F1.opExtrude","CAP_EDGE",EDGE,{"disambiguationData":[OSD([sQuery(id+"F0.wireOp",EDGE,"E4")])],"isStart":true});
            var Q199;
            {var subQ0=makeQuery(id+"F1.opExtrude","SWEPT_FACE",FACE,{"disambiguationData":[OSD([sQuery(id+"F0.wireOp",EDGE,"E3.2.0")])]});var subQ1=sQuery(id+"F4.wireOp",EDGE,"E32");var subQ2=sQuery(id+"F4.wireOp",EDGE,"E31");var subQ3=sQuery(id+"F2.wireOp",EDGE,"E19");var subQ4=sQuery(id+"F2.wireOp",EDGE,"E18");Q199=makeQuery(id+"F7.boolean.opBoolean","SPLIT",EDGE,{"disambiguationData":[topologyDisambiguationEdgeConnected([subQ0])],"derivedFrom":makeQuery(id+"F7.opPattern","COPY",EDGE,{"derivedFrom":makeQuery(id+"F6.opLoft","SWEPT_EDGE",EDGE,{"disambiguationData":[OSD([subQ4,subQ3,subQ2,subQ1])]}),"instanceName":"1"})});}
            var Q200;
            Q200=makeQuery(id+"F6.opLoft","MID_CAP_EDGE",EDGE,{"disambiguationData":[OSD([sQuery(id+"F4.wireOp",EDGE,"E25"),sQuery(id+"F4.wireOp",EDGE,"E29"),sQuery(id+"F4.wireOp",EDGE,"E30")])],"capPos":1.0});
            var Q201;
            Q201=makeQuery(id+"F6.opLoft","MID_CAP_EDGE",EDGE,{"disambiguationData":[OSD([sQuery(id+"F2.wireOp",EDGE,"E15"),sQuery(id+"F2.wireOp",EDGE,"E16"),sQuery(id+"F2.wireOp",EDGE,"E17")])],"capPos":0.0});
            var Q202;
            Q202=makeQuery(id+"F6.opLoft","SWEPT_EDGE",EDGE,{"disambiguationData":[OSD([sQuery(id+"F2.wireOp",EDGE,"E21"),sQuery(id+"F2.wireOp",EDGE,"E22"),sQuery(id+"F4.wireOp",EDGE,"E29"),sQuery(id+"F4.wireOp",EDGE,"E30")])]});
            var Q203;
            Q203=makeQuery(id+"F6.opLoft","MID_CAP_EDGE",EDGE,{"disambiguationData":[OSD([sQuery(id+"F2.wireOp",EDGE,"E19"),sQuery(id+"F2.wireOp",EDGE,"E20"),sQuery(id+"F2.wireOp",EDGE,"E21")])],"capPos":0.0});
            var Q204;
            Q204=makeQuery(id+"F6.opLoft","MID_CAP_EDGE",EDGE,{"disambiguationData":[OSD([sQuery(id+"F4.wireOp",EDGE,"E28"),sQuery(id+"F4.wireOp",EDGE,"E29"),sQuery(id+"F4.wireOp",EDGE,"E31")])],"capPos":1.0});
            var Q205;
            Q205=makeQuery(id+"F6.opLoft","MID_CAP_EDGE",EDGE,{"disambiguationData":[OSD([sQuery(id+"F2.wireOp",EDGE,"E20"),sQuery(id+"F2.wireOp",EDGE,"E21"),sQuery(id+"F2.wireOp",EDGE,"E22")])],"capPos":0.0});
            var Q206;
            Q206=makeQuery(id+"F6.opLoft","MID_CAP_EDGE",EDGE,{"disambiguationData":[OSD([sQuery(id+"F4.wireOp",EDGE,"E27"),sQuery(id+"F4.wireOp",EDGE,"E31"),sQuery(id+"F4.wireOp",EDGE,"E32")])],"capPos":1.0});
            var Q207;
            Q207=makeQuery(id+"F3.opExtrude","SWEPT_EDGE",EDGE,{"disambiguationData":[OSD([sQuery(id+"F2.wireOp",EDGE,"E15"),sQuery(id+"F2.wireOp",EDGE,"E22")])]});
            var Q208;
            Q208=makeQuery(id+"F3.opExtrude","SWEPT_EDGE",EDGE,{"disambiguationData":[OSD([sQuery(id+"F2.wireOp",EDGE,"E21"),sQuery(id+"F2.wireOp",EDGE,"E22")])]});
            var Q209;
            Q209=makeQuery(id+"F1.opExtrude","CAP_EDGE",EDGE,{"disambiguationData":[OSD([sQuery(id+"F0.wireOp",EDGE,"E2")])],"isStart":true});
            var Q210;
            Q210=makeQuery(id+"F1.opExtrude","CAP_EDGE",EDGE,{"disambiguationData":[OSD([sQuery(id+"F0.wireOp",EDGE,"E1")])],"isStart":true});
            var Q211;
            Q211=makeQuery(id+"F1.opExtrude","CAP_EDGE",EDGE,{"disambiguationData":[OSD([sQuery(id+"F0.wireOp",EDGE,"E3.3.3")])],"isStart":true});
            var Q212;
            Q212=makeQuery(id+"F6.opLoft","MID_CAP_EDGE",EDGE,{"disambiguationData":[OSD([sQuery(id+"F4.wireOp",EDGE,"E25"),sQuery(id+"F4.wireOp",EDGE,"E26"),sQuery(id+"F4.wireOp",EDGE,"E30")])],"capPos":1.0});
            var Q213;
            Q213=makeQuery(id+"F6.opLoft","MID_CAP_EDGE",EDGE,{"disambiguationData":[OSD([sQuery(id+"F2.wireOp",EDGE,"E15"),sQuery(id+"F2.wireOp",EDGE,"E16"),sQuery(id+"F2.wireOp",EDGE,"E22")])],"capPos":0.0});
            var Q214;
            Q214=makeQuery(id+"F6.opLoft","SWEPT_EDGE",EDGE,{"disambiguationData":[OSD([sQuery(id+"F2.wireOp",EDGE,"E15"),sQuery(id+"F2.wireOp",EDGE,"E22"),sQuery(id+"F4.wireOp",EDGE,"E25"),sQuery(id+"F4.wireOp",EDGE,"E30")])]});
            var Q215;
            Q215=makeQuery(id+"F6.opLoft","MID_CAP_EDGE",EDGE,{"disambiguationData":[OSD([sQuery(id+"F2.wireOp",EDGE,"E15"),sQuery(id+"F2.wireOp",EDGE,"E21"),sQuery(id+"F2.wireOp",EDGE,"E22")])],"capPos":0.0});
            fillet(context, id + "F8", {"entities" : qUnion([Q0, Q1, Q2, Q3, Q4, Q5, Q6, Q7, Q8, Q9, Q10, Q11, Q12, Q13, Q14, Q15, Q16, Q17, Q18, Q19, Q20, Q21, Q22, Q23, Q24, Q25, Q26, Q27, Q28, Q29, Q30, Q31, Q32, Q33, Q34, Q35, Q36, Q37, Q38, Q39, Q40, Q41, Q42, Q43, Q44, Q45, Q46, Q47, Q48, Q49, Q50, Q51, Q52, Q53, Q54, Q55, Q56, Q57, Q58, Q59, Q60, Q61, Q62, Q63, Q64, Q65, Q66, Q67, Q68, Q69, Q70, Q71, Q72, Q73, Q74, Q75, Q76, Q77, Q78, Q79, Q80, Q81, Q82, Q83, Q84, Q85, Q86, Q87, Q88, Q89, Q90, Q91, Q92, Q93, Q94, Q95, Q96, Q97, Q98, Q99, Q100, Q101, Q102, Q103, Q104, Q105, Q106, Q107, Q108, Q109, Q110, Q111, Q112, Q113, Q114, Q115, Q116, Q117, Q118, Q119, Q120, Q121, Q122, Q123, Q124, Q125, Q126, Q127, Q128, Q129, Q130, Q131, Q132, Q133, Q134, Q135, Q136, Q137, Q138, Q139, Q140, Q141, Q142, Q143, Q144, Q145, Q146, Q147, Q148, Q149, Q150, Q151, Q152, Q153, Q154, Q155, Q156, Q157, Q158, Q159, Q160, Q161, Q162, Q163, Q164, Q165, Q166, Q167, Q168, Q169, Q170, Q171, Q172, Q173, Q174, Q175, Q176, Q177, Q178, Q179, Q180, Q181, Q182, Q183, Q184, Q185, Q186, Q187, Q188, Q189, Q190, Q191, Q192, Q193, Q194, Q195, Q196, Q197, Q198, Q199, Q200, Q201, Q202, Q203, Q204, Q205, Q206, Q207, Q208, Q209, Q210, Q211, Q212, Q213, Q214, Q215]), "radius" : 5 * mm, "tangentPropagation" : true, "allowEdgeOverflow" : false});
        }
    });
